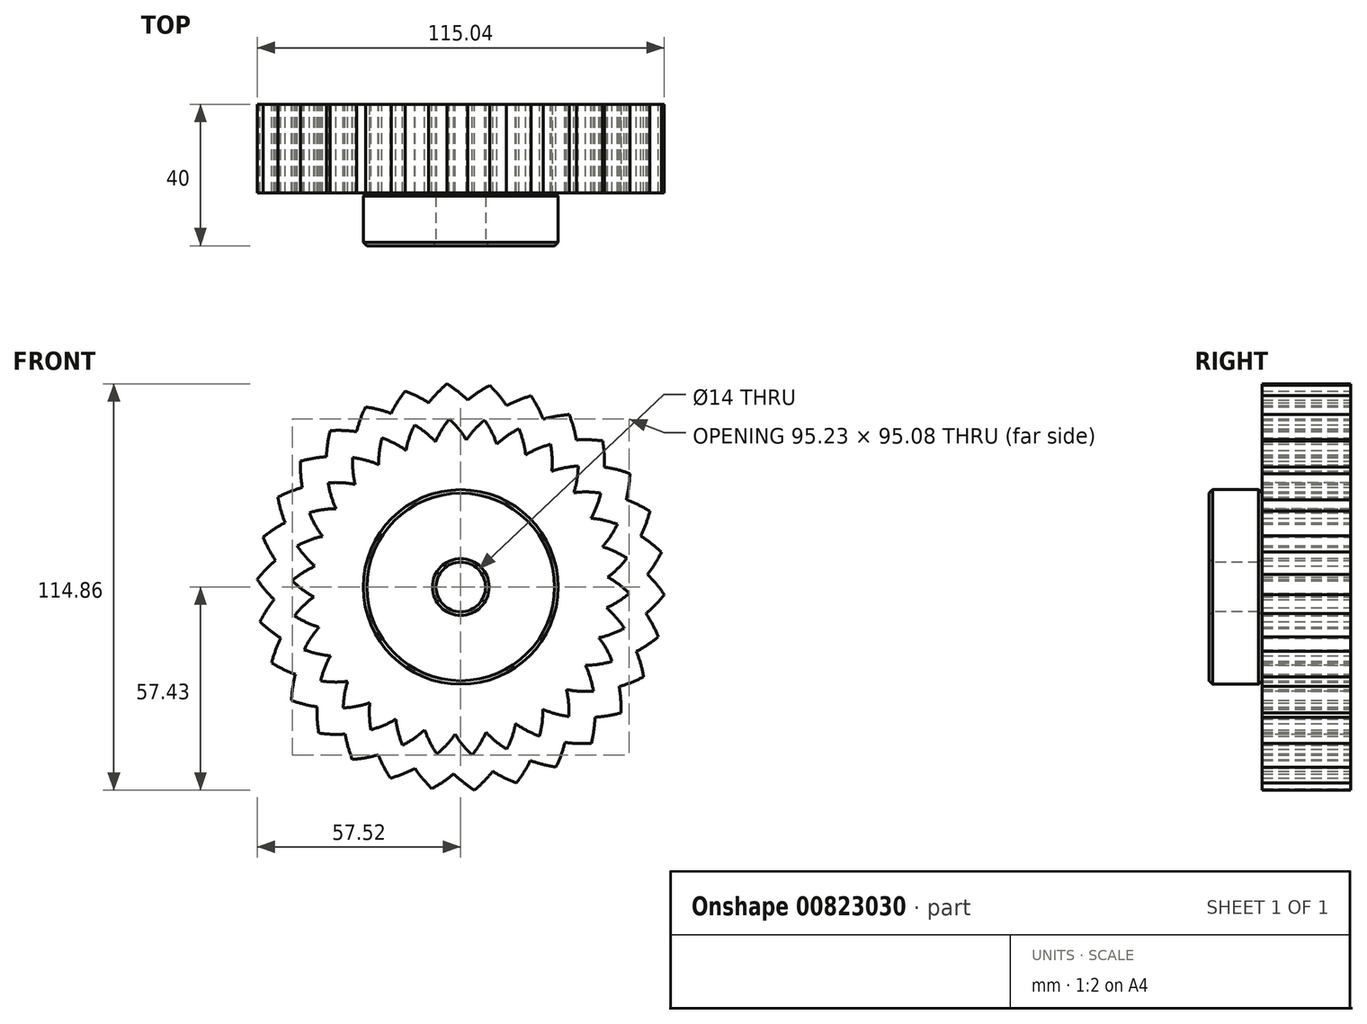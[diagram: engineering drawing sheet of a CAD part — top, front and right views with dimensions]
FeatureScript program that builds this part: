
annotation { "Feature Type Name" : "Feature", "Feature Type Description" : "" }
export const myFeature = defineFeature(function(context is Context, id is Id, definition is map)
    precondition{}
    {
        {
            var Q0;
            Q0=qCreatedBy(makeId("Front.planeOp"),FACE);
            var sketch = newSketch(context, id + "F0", { "sketchPlane" : qUnion([Q0])});
            skArc(sketch, "E0", {"start": v(-34.7, 6.12) * mm, "mid": v(-35.1, 3.07) * mm, "end": v(-35.24, 0) * mm, "construction": true});
            skLineSegment(sketch, "E1", {"start": v(0, 0) * mm, "end": v(309.01, 0) * mm, "construction": true});
            skPoint(sketch, "E2", {"position": v(35.24, 0) * mm});
            skLineSegment(sketch, "E3", {"start": v(0, 0) * mm, "end": v(-35.24, 0) * mm, "construction": true});
            skArc(sketch, "E4.trimOffspring", {"start": v(-30.6, -17.46) * mm, "mid": v(35.03, 3.83) * mm, "end": v(-33.66, 10.43) * mm, "construction": true});
            skFitSpline(sketch, "E5", {"points": [v(35.24, 0) * mm, v(35.77, 0.06) * mm, v(37.32, 0.5) * mm, v(39.74, 1.64) * mm, v(42.8, 3.8) * mm, v(46.2, 7.23) * mm, v(49.58, 12.07) * mm, v(52.5, 18.39) * mm, v(54.57, 26.16) * mm], "startDerivative": vector(10.04, 0.75) * mm, "endDerivative": vector(10.04, 44.08) * mm});
            skArc(sketch, "E6", {"start": v(34.12, 5.1) * mm, "mid": v(34, 5.9) * mm, "end": v(33.85, 6.7) * mm});
            skArc(sketch, "E7", {"start": v(39.96, 1.77) * mm, "mid": v(39.9, 2.68) * mm, "end": v(39.84, 3.6) * mm});
            skCircle(sketch, "E8", {"center": v(0, 0) * mm, "radius": 37.5 * mm, "construction": true});
            skPoint(sketch, "E9", {"position": v(37.5, 0.56) * mm});
            skPoint(sketch, "E10", {"position": v(36.56, 8.34) * mm});
            skPoint(sketch, "E11.orphan", {"position": v(37.03, 4.45) * mm});
            skLineSegment(sketch, "E12", {"start": v(37.5, 0.56) * mm, "end": v(37.03, 4.45) * mm, "construction": true});
            skLineSegment(sketch, "E13", {"start": v(37.26, 2.5) * mm, "end": v(0, 0) * mm, "construction": true});
            skFitSpline(sketch, "E14.MirrorCS", {"points": [v(34.92, 4.72) * mm, v(35.46, 4.73) * mm, v(37.05, 4.5) * mm, v(39.6, 3.7) * mm, v(42.93, 1.96) * mm, v(46.76, -0.98) * mm, v(50.74, -5.32) * mm, v(54.5, -11.2) * mm, v(57.58, -18.62) * mm], "startDerivative": vector(10.05, 0.6) * mm, "endDerivative": vector(15.85, -42.34) * mm});
            skLineSegment(sketch, "E15", {"start": v(35.24, 0) * mm, "end": v(35, 0) * mm});
            skLineSegment(sketch, "E16.MirrorCS", {"start": v(34.92, 4.72) * mm, "end": v(34.68, 4.68) * mm});
            skPoint(sketch, "E17.visualSharp", {"position": v(34.19, 4.62) * mm});
            skArc(sketch, "E17.filletArc", {"start": v(34.12, 5.1) * mm, "mid": v(34.31, 4.78) * mm, "end": v(34.68, 4.68) * mm});
            skPoint(sketch, "E18.visualSharp", {"position": v(34.5, 0) * mm});
            skArc(sketch, "E18.filletArc", {"start": v(35, 0) * mm, "mid": v(34.65, -0.14) * mm, "end": v(34.5, -0.5) * mm});
            skPoint(sketch, "E19.1.1", {"position": v(34.47, 7.33) * mm});
            skPoint(sketch, "E19.1.2", {"position": v(33.75, 7.17) * mm});
            skPoint(sketch, "E19.1.3", {"position": v(32.48, 11.62) * mm});
            skPoint(sketch, "E19.1.4", {"position": v(35.3, 12.05) * mm});
            skPoint(sketch, "E19.1.5", {"position": v(33.18, 11.87) * mm});
            skArc(sketch, "E19.1.6", {"start": v(38.72, 10.04) * mm, "mid": v(38.48, 10.92) * mm, "end": v(38.22, 11.8) * mm});
            skArc(sketch, "E19.1.8", {"start": v(32.31, 12.09) * mm, "mid": v(32.57, 11.8) * mm, "end": v(32.95, 11.8) * mm});
            skPoint(sketch, "E19.1.9", {"position": v(34.47, 7.33) * mm});
            skPoint(sketch, "E19.1.10", {"position": v(33.18, 11.87) * mm});
            skArc(sketch, "E19.1.11", {"start": v(34.23, 7.28) * mm, "mid": v(33.92, 7.06) * mm, "end": v(33.85, 6.7) * mm});
            skPoint(sketch, "E19.1.12", {"position": v(33.18, 11.87) * mm});
            skPoint(sketch, "E19.1.13", {"position": v(34.47, 7.33) * mm});
            skPoint(sketch, "E19.1.14", {"position": v(33.18, 11.87) * mm});
            skPoint(sketch, "E19.1.15", {"position": v(34.47, 7.33) * mm});
            skPoint(sketch, "E19.1.16", {"position": v(34.47, 7.33) * mm});
            skPoint(sketch, "E19.1.17", {"position": v(33.18, 11.87) * mm});
            skPoint(sketch, "E19.1.18", {"position": v(33.18, 11.87) * mm});
            skPoint(sketch, "E19.1.19", {"position": v(34.47, 7.33) * mm});
            skPoint(sketch, "E19.1.20", {"position": v(33.18, 11.87) * mm});
            skPoint(sketch, "E19.1.21", {"position": v(34.47, 7.33) * mm});
            skPoint(sketch, "E19.1.22", {"position": v(33.18, 11.87) * mm});
            skPoint(sketch, "E19.1.23", {"position": v(34.47, 7.33) * mm});
            skLineSegment(sketch, "E19.1.24", {"start": v(33.18, 11.87) * mm, "end": v(32.95, 11.8) * mm});
            skLineSegment(sketch, "E19.1.25", {"start": v(34.47, 7.33) * mm, "end": v(34.23, 7.28) * mm});
            skPoint(sketch, "E19.2.1", {"position": v(32.2, 14.33) * mm});
            skPoint(sketch, "E19.2.2", {"position": v(31.52, 14.03) * mm});
            skPoint(sketch, "E19.2.3", {"position": v(29.36, 18.12) * mm});
            skPoint(sketch, "E19.2.4", {"position": v(32.02, 19.13) * mm});
            skPoint(sketch, "E19.2.5", {"position": v(29.98, 18.51) * mm});
            skArc(sketch, "E19.2.6", {"start": v(35.79, 17.87) * mm, "mid": v(35.37, 18.68) * mm, "end": v(34.93, 19.49) * mm});
            skPoint(sketch, "E19.2.7", {"position": v(34.03, 15.76) * mm});
            skArc(sketch, "E19.2.8", {"start": v(29.1, 18.54) * mm, "mid": v(29.4, 18.32) * mm, "end": v(29.78, 18.38) * mm});
            skPoint(sketch, "E19.2.9", {"position": v(32.2, 14.33) * mm});
            skPoint(sketch, "E19.2.10", {"position": v(29.98, 18.51) * mm});
            skArc(sketch, "E19.2.11", {"start": v(31.97, 14.23) * mm, "mid": v(31.7, 13.96) * mm, "end": v(31.71, 13.58) * mm});
            skPoint(sketch, "E19.2.12", {"position": v(29.98, 18.51) * mm});
            skPoint(sketch, "E19.2.13", {"position": v(32.2, 14.33) * mm});
            skPoint(sketch, "E19.2.14", {"position": v(29.98, 18.51) * mm});
            skPoint(sketch, "E19.2.15", {"position": v(32.2, 14.33) * mm});
            skPoint(sketch, "E19.2.16", {"position": v(32.2, 14.33) * mm});
            skPoint(sketch, "E19.2.17", {"position": v(29.98, 18.51) * mm});
            skPoint(sketch, "E19.2.18", {"position": v(29.98, 18.51) * mm});
            skPoint(sketch, "E19.2.19", {"position": v(32.2, 14.33) * mm});
            skPoint(sketch, "E19.2.20", {"position": v(29.98, 18.51) * mm});
            skPoint(sketch, "E19.2.21", {"position": v(32.2, 14.33) * mm});
            skPoint(sketch, "E19.2.22", {"position": v(29.98, 18.51) * mm});
            skPoint(sketch, "E19.2.23", {"position": v(32.2, 14.33) * mm});
            skLineSegment(sketch, "E19.2.24", {"start": v(29.98, 18.51) * mm, "end": v(29.78, 18.38) * mm});
            skLineSegment(sketch, "E19.2.25", {"start": v(32.2, 14.33) * mm, "end": v(31.97, 14.23) * mm});
            skLineSegment(sketch, "E19.3.0", {"start": v(30, 22.5) * mm, "end": v(27.34, 25.37) * mm, "construction": true});
            skPoint(sketch, "E19.3.1", {"position": v(28.5, 20.71) * mm});
            skPoint(sketch, "E19.3.2", {"position": v(27.91, 20.28) * mm});
            skPoint(sketch, "E19.3.3", {"position": v(24.95, 23.83) * mm});
            skPoint(sketch, "E19.3.4", {"position": v(27.34, 25.37) * mm});
            skPoint(sketch, "E19.3.5", {"position": v(25.48, 24.34) * mm});
            skArc(sketch, "E19.3.6", {"start": v(31.29, 24.92) * mm, "mid": v(30.71, 25.63) * mm, "end": v(30.12, 26.32) * mm});
            skPoint(sketch, "E19.3.7", {"position": v(30, 22.5) * mm});
            skArc(sketch, "E19.3.8", {"start": v(24.6, 24.19) * mm, "mid": v(24.95, 24.04) * mm, "end": v(25.3, 24.17) * mm});
            skPoint(sketch, "E19.3.9", {"position": v(28.5, 20.71) * mm});
            skPoint(sketch, "E19.3.10", {"position": v(25.48, 24.34) * mm});
            skArc(sketch, "E19.3.11", {"start": v(28.31, 20.57) * mm, "mid": v(28.11, 20.25) * mm, "end": v(28.2, 19.88) * mm});
            skPoint(sketch, "E19.3.12", {"position": v(25.48, 24.34) * mm});
            skPoint(sketch, "E19.3.13", {"position": v(28.5, 20.71) * mm});
            skPoint(sketch, "E19.3.14", {"position": v(25.48, 24.34) * mm});
            skPoint(sketch, "E19.3.15", {"position": v(28.5, 20.71) * mm});
            skPoint(sketch, "E19.3.16", {"position": v(28.5, 20.71) * mm});
            skPoint(sketch, "E19.3.17", {"position": v(25.48, 24.34) * mm});
            skPoint(sketch, "E19.3.18", {"position": v(25.48, 24.34) * mm});
            skPoint(sketch, "E19.3.19", {"position": v(28.5, 20.71) * mm});
            skPoint(sketch, "E19.3.20", {"position": v(25.48, 24.34) * mm});
            skPoint(sketch, "E19.3.21", {"position": v(28.5, 20.71) * mm});
            skPoint(sketch, "E19.3.22", {"position": v(25.48, 24.34) * mm});
            skPoint(sketch, "E19.3.23", {"position": v(28.5, 20.71) * mm});
            skLineSegment(sketch, "E19.3.24", {"start": v(25.48, 24.34) * mm, "end": v(25.3, 24.17) * mm});
            skLineSegment(sketch, "E19.3.25", {"start": v(28.5, 20.71) * mm, "end": v(28.31, 20.57) * mm});
            skLineSegment(sketch, "E19.4.0", {"start": v(24.67, 28.24) * mm, "end": v(21.47, 30.5) * mm, "construction": true});
            skPoint(sketch, "E19.4.1", {"position": v(23.58, 26.19) * mm});
            skPoint(sketch, "E19.4.2", {"position": v(23.09, 25.64) * mm});
            skPoint(sketch, "E19.4.3", {"position": v(19.45, 28.5) * mm});
            skPoint(sketch, "E19.4.4", {"position": v(21.47, 30.5) * mm});
            skPoint(sketch, "E19.4.5", {"position": v(19.86, 29.1) * mm});
            skArc(sketch, "E19.4.6", {"start": v(25.42, 30.88) * mm, "mid": v(24.71, 31.45) * mm, "end": v(23.99, 32.01) * mm});
            skPoint(sketch, "E19.4.7", {"position": v(24.67, 28.24) * mm});
            skArc(sketch, "E19.4.8", {"start": v(19.04, 28.77) * mm, "mid": v(19.4, 28.7) * mm, "end": v(19.73, 28.9) * mm});
            skPoint(sketch, "E19.4.9", {"position": v(23.58, 26.19) * mm});
            skPoint(sketch, "E19.4.10", {"position": v(19.86, 29.1) * mm});
            skArc(sketch, "E19.4.11", {"start": v(23.42, 26) * mm, "mid": v(23.29, 25.65) * mm, "end": v(23.45, 25.3) * mm});
            skPoint(sketch, "E19.4.12", {"position": v(19.86, 29.1) * mm});
            skPoint(sketch, "E19.4.13", {"position": v(23.58, 26.19) * mm});
            skPoint(sketch, "E19.4.14", {"position": v(19.86, 29.1) * mm});
            skPoint(sketch, "E19.4.15", {"position": v(23.58, 26.19) * mm});
            skPoint(sketch, "E19.4.16", {"position": v(23.58, 26.19) * mm});
            skPoint(sketch, "E19.4.17", {"position": v(19.86, 29.1) * mm});
            skPoint(sketch, "E19.4.18", {"position": v(19.86, 29.1) * mm});
            skPoint(sketch, "E19.4.19", {"position": v(23.58, 26.19) * mm});
            skPoint(sketch, "E19.4.20", {"position": v(19.86, 29.1) * mm});
            skPoint(sketch, "E19.4.21", {"position": v(23.58, 26.19) * mm});
            skPoint(sketch, "E19.4.22", {"position": v(19.86, 29.1) * mm});
            skPoint(sketch, "E19.4.23", {"position": v(23.58, 26.19) * mm});
            skLineSegment(sketch, "E19.4.24", {"start": v(19.86, 29.1) * mm, "end": v(19.73, 28.9) * mm});
            skLineSegment(sketch, "E19.4.25", {"start": v(23.58, 26.19) * mm, "end": v(23.42, 26) * mm});
            skLineSegment(sketch, "E19.5.0", {"start": v(18.26, 32.75) * mm, "end": v(14.66, 34.3) * mm, "construction": true});
            skPoint(sketch, "E19.5.1", {"position": v(17.62, 30.52) * mm});
            skPoint(sketch, "E19.5.2", {"position": v(17.25, 29.88) * mm});
            skPoint(sketch, "E19.5.3", {"position": v(13.1, 31.92) * mm});
            skPoint(sketch, "E19.5.4", {"position": v(14.66, 34.3) * mm});
            skPoint(sketch, "E19.5.5", {"position": v(13.38, 32.6) * mm});
            skArc(sketch, "E19.5.6", {"start": v(18.45, 35.5) * mm, "mid": v(17.63, 35.9) * mm, "end": v(16.8, 36.3) * mm});
            skPoint(sketch, "E19.5.7", {"position": v(18.26, 32.75) * mm});
            skArc(sketch, "E19.5.8", {"start": v(12.64, 32.1) * mm, "mid": v(13.02, 32.1) * mm, "end": v(13.28, 32.38) * mm});
            skPoint(sketch, "E19.5.9", {"position": v(17.62, 30.52) * mm});
            skPoint(sketch, "E19.5.10", {"position": v(13.38, 32.6) * mm});
            skArc(sketch, "E19.5.11", {"start": v(17.5, 30.3) * mm, "mid": v(17.45, 29.93) * mm, "end": v(17.68, 29.63) * mm});
            skPoint(sketch, "E19.5.12", {"position": v(13.38, 32.6) * mm});
            skPoint(sketch, "E19.5.13", {"position": v(17.62, 30.52) * mm});
            skPoint(sketch, "E19.5.14", {"position": v(13.38, 32.6) * mm});
            skPoint(sketch, "E19.5.15", {"position": v(17.62, 30.52) * mm});
            skPoint(sketch, "E19.5.16", {"position": v(17.62, 30.52) * mm});
            skPoint(sketch, "E19.5.17", {"position": v(13.38, 32.6) * mm});
            skPoint(sketch, "E19.5.18", {"position": v(13.38, 32.6) * mm});
            skPoint(sketch, "E19.5.19", {"position": v(17.62, 30.52) * mm});
            skPoint(sketch, "E19.5.20", {"position": v(13.38, 32.6) * mm});
            skPoint(sketch, "E19.5.21", {"position": v(17.62, 30.52) * mm});
            skPoint(sketch, "E19.5.22", {"position": v(13.38, 32.6) * mm});
            skPoint(sketch, "E19.5.23", {"position": v(17.62, 30.52) * mm});
            skLineSegment(sketch, "E19.5.24", {"start": v(13.38, 32.6) * mm, "end": v(13.28, 32.38) * mm});
            skLineSegment(sketch, "E19.5.25", {"start": v(17.62, 30.52) * mm, "end": v(17.5, 30.3) * mm});
            skLineSegment(sketch, "E19.6.0", {"start": v(11.06, 35.83) * mm, "end": v(7.2, 36.6) * mm, "construction": true});
            skPoint(sketch, "E19.6.1", {"position": v(10.89, 33.51) * mm});
            skPoint(sketch, "E19.6.2", {"position": v(10.66, 32.81) * mm});
            skPoint(sketch, "E19.6.3", {"position": v(6.17, 33.94) * mm});
            skPoint(sketch, "E19.6.4", {"position": v(7.2, 36.6) * mm});
            skPoint(sketch, "E19.6.5", {"position": v(6.3, 34.67) * mm});
            skArc(sketch, "E19.6.6", {"start": v(10.67, 38.55) * mm, "mid": v(9.78, 38.79) * mm, "end": v(8.9, 39) * mm});
            skPoint(sketch, "E19.6.7", {"position": v(11.06, 35.83) * mm});
            skArc(sketch, "E19.6.8", {"start": v(5.69, 34.03) * mm, "mid": v(6.06, 34.11) * mm, "end": v(6.26, 34.43) * mm});
            skPoint(sketch, "E19.6.9", {"position": v(10.89, 33.51) * mm});
            skPoint(sketch, "E19.6.10", {"position": v(6.3, 34.67) * mm});
            skArc(sketch, "E19.6.11", {"start": v(10.81, 33.28) * mm, "mid": v(10.84, 32.9) * mm, "end": v(11.13, 32.66) * mm});
            skPoint(sketch, "E19.6.12", {"position": v(6.3, 34.67) * mm});
            skPoint(sketch, "E19.6.13", {"position": v(10.89, 33.51) * mm});
            skPoint(sketch, "E19.6.14", {"position": v(6.3, 34.67) * mm});
            skPoint(sketch, "E19.6.15", {"position": v(10.89, 33.51) * mm});
            skPoint(sketch, "E19.6.16", {"position": v(10.89, 33.51) * mm});
            skPoint(sketch, "E19.6.17", {"position": v(6.3, 34.67) * mm});
            skPoint(sketch, "E19.6.18", {"position": v(6.3, 34.67) * mm});
            skPoint(sketch, "E19.6.19", {"position": v(10.89, 33.51) * mm});
            skPoint(sketch, "E19.6.20", {"position": v(6.3, 34.67) * mm});
            skPoint(sketch, "E19.6.21", {"position": v(10.89, 33.51) * mm});
            skPoint(sketch, "E19.6.22", {"position": v(6.3, 34.67) * mm});
            skPoint(sketch, "E19.6.23", {"position": v(10.89, 33.51) * mm});
            skLineSegment(sketch, "E19.6.24", {"start": v(6.3, 34.67) * mm, "end": v(6.26, 34.43) * mm});
            skLineSegment(sketch, "E19.6.25", {"start": v(10.89, 33.51) * mm, "end": v(10.81, 33.28) * mm});
            skLineSegment(sketch, "E19.7.0", {"start": v(3.36, 37.35) * mm, "end": v(-0.56, 37.3) * mm, "construction": true});
            skPoint(sketch, "E19.7.1", {"position": v(3.68, 35.05) * mm});
            skPoint(sketch, "E19.7.2", {"position": v(3.6, 34.31) * mm});
            skPoint(sketch, "E19.7.3", {"position": v(-1.02, 34.48) * mm});
            skPoint(sketch, "E19.7.4", {"position": v(-0.56, 37.3) * mm});
            skPoint(sketch, "E19.7.5", {"position": v(-1.04, 35.22) * mm});
            skArc(sketch, "E19.7.6", {"start": v(2.42, 39.93) * mm, "mid": v(1.5, 39.97) * mm, "end": v(0.6, 40) * mm});
            skPoint(sketch, "E19.7.7", {"position": v(3.36, 37.35) * mm});
            skArc(sketch, "E19.7.8", {"start": v(-1.51, 34.47) * mm, "mid": v(-1.17, 34.63) * mm, "end": v(-1.03, 34.98) * mm});
            skPoint(sketch, "E19.7.9", {"position": v(3.68, 35.05) * mm});
            skPoint(sketch, "E19.7.10", {"position": v(-1.04, 35.22) * mm});
            skArc(sketch, "E19.7.11", {"start": v(3.66, 34.8) * mm, "mid": v(3.76, 34.44) * mm, "end": v(4.1, 34.26) * mm});
            skPoint(sketch, "E19.7.12", {"position": v(-1.04, 35.22) * mm});
            skPoint(sketch, "E19.7.13", {"position": v(3.68, 35.05) * mm});
            skPoint(sketch, "E19.7.14", {"position": v(-1.04, 35.22) * mm});
            skPoint(sketch, "E19.7.15", {"position": v(3.68, 35.05) * mm});
            skPoint(sketch, "E19.7.16", {"position": v(3.68, 35.05) * mm});
            skPoint(sketch, "E19.7.17", {"position": v(-1.04, 35.22) * mm});
            skPoint(sketch, "E19.7.18", {"position": v(-1.04, 35.22) * mm});
            skPoint(sketch, "E19.7.19", {"position": v(3.68, 35.05) * mm});
            skPoint(sketch, "E19.7.20", {"position": v(-1.04, 35.22) * mm});
            skPoint(sketch, "E19.7.21", {"position": v(3.68, 35.05) * mm});
            skPoint(sketch, "E19.7.22", {"position": v(-1.04, 35.22) * mm});
            skPoint(sketch, "E19.7.23", {"position": v(3.68, 35.05) * mm});
            skLineSegment(sketch, "E19.7.24", {"start": v(-1.04, 35.22) * mm, "end": v(-1.03, 34.98) * mm});
            skLineSegment(sketch, "E19.7.25", {"start": v(3.68, 35.05) * mm, "end": v(3.66, 34.8) * mm});
            skLineSegment(sketch, "E19.8.0", {"start": v(-4.47, 37.23) * mm, "end": v(-8.3, 36.36) * mm, "construction": true});
            skPoint(sketch, "E19.8.1", {"position": v(-3.68, 35.05) * mm});
            skPoint(sketch, "E19.8.2", {"position": v(-3.6, 34.31) * mm});
            skPoint(sketch, "E19.8.3", {"position": v(-8.17, 33.52) * mm});
            skPoint(sketch, "E19.8.4", {"position": v(-8.3, 36.36) * mm});
            skPoint(sketch, "E19.8.5", {"position": v(-8.34, 34.24) * mm});
            skArc(sketch, "E19.8.6", {"start": v(-5.94, 39.56) * mm, "mid": v(-6.84, 39.41) * mm, "end": v(-7.74, 39.24) * mm});
            skPoint(sketch, "E19.8.7", {"position": v(-4.47, 37.23) * mm});
            skArc(sketch, "E19.8.8", {"start": v(-8.64, 33.4) * mm, "mid": v(-8.34, 33.63) * mm, "end": v(-8.28, 34) * mm});
            skPoint(sketch, "E19.8.9", {"position": v(-3.68, 35.05) * mm});
            skPoint(sketch, "E19.8.10", {"position": v(-8.34, 34.24) * mm});
            skArc(sketch, "E19.8.11", {"start": v(-3.66, 34.8) * mm, "mid": v(-3.48, 34.47) * mm, "end": v(-3.12, 34.36) * mm});
            skPoint(sketch, "E19.8.12", {"position": v(-8.34, 34.24) * mm});
            skPoint(sketch, "E19.8.13", {"position": v(-3.68, 35.05) * mm});
            skPoint(sketch, "E19.8.14", {"position": v(-8.34, 34.24) * mm});
            skPoint(sketch, "E19.8.15", {"position": v(-3.68, 35.05) * mm});
            skPoint(sketch, "E19.8.16", {"position": v(-3.68, 35.05) * mm});
            skPoint(sketch, "E19.8.17", {"position": v(-8.34, 34.24) * mm});
            skPoint(sketch, "E19.8.18", {"position": v(-8.34, 34.24) * mm});
            skPoint(sketch, "E19.8.19", {"position": v(-3.68, 35.05) * mm});
            skPoint(sketch, "E19.8.20", {"position": v(-8.34, 34.24) * mm});
            skPoint(sketch, "E19.8.21", {"position": v(-3.68, 35.05) * mm});
            skPoint(sketch, "E19.8.22", {"position": v(-8.34, 34.24) * mm});
            skPoint(sketch, "E19.8.23", {"position": v(-3.68, 35.05) * mm});
            skLineSegment(sketch, "E19.8.24", {"start": v(-8.34, 34.24) * mm, "end": v(-8.28, 34) * mm});
            skLineSegment(sketch, "E19.8.25", {"start": v(-3.68, 35.05) * mm, "end": v(-3.66, 34.8) * mm});
            skLineSegment(sketch, "E19.9.0", {"start": v(-12.12, 35.49) * mm, "end": v(-15.67, 33.84) * mm, "construction": true});
            skPoint(sketch, "E19.9.1", {"position": v(-10.89, 33.51) * mm});
            skPoint(sketch, "E19.9.2", {"position": v(-10.66, 32.81) * mm});
            skPoint(sketch, "E19.9.3", {"position": v(-14.96, 31.09) * mm});
            skPoint(sketch, "E19.9.4", {"position": v(-15.67, 33.84) * mm});
            skPoint(sketch, "E19.9.5", {"position": v(-15.28, 31.76) * mm});
            skArc(sketch, "E19.9.6", {"start": v(-14.03, 37.46) * mm, "mid": v(-14.88, 37.13) * mm, "end": v(-15.73, 36.78) * mm});
            skPoint(sketch, "E19.9.7", {"position": v(-12.12, 35.49) * mm});
            skArc(sketch, "E19.9.8", {"start": v(-15.4, 30.87) * mm, "mid": v(-15.15, 31.16) * mm, "end": v(-15.17, 31.54) * mm});
            skPoint(sketch, "E19.9.9", {"position": v(-10.89, 33.51) * mm});
            skPoint(sketch, "E19.9.10", {"position": v(-15.28, 31.76) * mm});
            skArc(sketch, "E19.9.11", {"start": v(-10.81, 33.28) * mm, "mid": v(-10.57, 33) * mm, "end": v(-10.2, 32.96) * mm});
            skPoint(sketch, "E19.9.12", {"position": v(-15.28, 31.76) * mm});
            skPoint(sketch, "E19.9.13", {"position": v(-10.89, 33.51) * mm});
            skPoint(sketch, "E19.9.14", {"position": v(-15.28, 31.76) * mm});
            skPoint(sketch, "E19.9.15", {"position": v(-10.89, 33.51) * mm});
            skPoint(sketch, "E19.9.16", {"position": v(-10.89, 33.51) * mm});
            skPoint(sketch, "E19.9.17", {"position": v(-15.28, 31.76) * mm});
            skPoint(sketch, "E19.9.18", {"position": v(-15.28, 31.76) * mm});
            skPoint(sketch, "E19.9.19", {"position": v(-10.89, 33.51) * mm});
            skPoint(sketch, "E19.9.20", {"position": v(-15.28, 31.76) * mm});
            skPoint(sketch, "E19.9.21", {"position": v(-10.89, 33.51) * mm});
            skPoint(sketch, "E19.9.22", {"position": v(-15.28, 31.76) * mm});
            skPoint(sketch, "E19.9.23", {"position": v(-10.89, 33.51) * mm});
            skLineSegment(sketch, "E19.9.24", {"start": v(-15.28, 31.76) * mm, "end": v(-15.17, 31.54) * mm});
            skLineSegment(sketch, "E19.9.25", {"start": v(-10.89, 33.51) * mm, "end": v(-10.81, 33.28) * mm});
            skLineSegment(sketch, "E19.10.0", {"start": v(-19.23, 32.2) * mm, "end": v(-22.37, 29.84) * mm, "construction": true});
            skPoint(sketch, "E19.10.1", {"position": v(-17.62, 30.52) * mm});
            skPoint(sketch, "E19.10.2", {"position": v(-17.25, 29.88) * mm});
            skPoint(sketch, "E19.10.3", {"position": v(-21.1, 27.3) * mm});
            skPoint(sketch, "E19.10.4", {"position": v(-22.37, 29.84) * mm});
            skPoint(sketch, "E19.10.5", {"position": v(-21.54, 27.89) * mm});
            skArc(sketch, "E19.10.6", {"start": v(-21.51, 33.72) * mm, "mid": v(-22.28, 33.22) * mm, "end": v(-23.03, 32.7) * mm});
            skPoint(sketch, "E19.10.7", {"position": v(-19.23, 32.2) * mm});
            skArc(sketch, "E19.10.8", {"start": v(-21.48, 27) * mm, "mid": v(-21.3, 27.33) * mm, "end": v(-21.4, 27.7) * mm});
            skPoint(sketch, "E19.10.9", {"position": v(-17.62, 30.52) * mm});
            skPoint(sketch, "E19.10.10", {"position": v(-21.54, 27.89) * mm});
            skArc(sketch, "E19.10.11", {"start": v(-17.5, 30.3) * mm, "mid": v(-17.2, 30.08) * mm, "end": v(-16.82, 30.12) * mm});
            skPoint(sketch, "E19.10.12", {"position": v(-21.54, 27.89) * mm});
            skPoint(sketch, "E19.10.13", {"position": v(-17.62, 30.52) * mm});
            skPoint(sketch, "E19.10.14", {"position": v(-21.54, 27.89) * mm});
            skPoint(sketch, "E19.10.15", {"position": v(-17.62, 30.52) * mm});
            skPoint(sketch, "E19.10.16", {"position": v(-17.62, 30.52) * mm});
            skPoint(sketch, "E19.10.17", {"position": v(-21.54, 27.89) * mm});
            skPoint(sketch, "E19.10.18", {"position": v(-21.54, 27.89) * mm});
            skPoint(sketch, "E19.10.19", {"position": v(-17.62, 30.52) * mm});
            skPoint(sketch, "E19.10.20", {"position": v(-21.54, 27.89) * mm});
            skPoint(sketch, "E19.10.21", {"position": v(-17.62, 30.52) * mm});
            skPoint(sketch, "E19.10.22", {"position": v(-21.54, 27.89) * mm});
            skPoint(sketch, "E19.10.23", {"position": v(-17.62, 30.52) * mm});
            skLineSegment(sketch, "E19.10.24", {"start": v(-21.54, 27.89) * mm, "end": v(-21.4, 27.7) * mm});
            skLineSegment(sketch, "E19.10.25", {"start": v(-17.62, 30.52) * mm, "end": v(-17.5, 30.3) * mm});
            skLineSegment(sketch, "E19.11.0", {"start": v(-25.5, 27.5) * mm, "end": v(-28.08, 24.54) * mm, "construction": true});
            skPoint(sketch, "E19.11.1", {"position": v(-23.58, 26.19) * mm});
            skPoint(sketch, "E19.11.2", {"position": v(-23.09, 25.64) * mm});
            skPoint(sketch, "E19.11.3", {"position": v(-26.3, 22.32) * mm});
            skPoint(sketch, "E19.11.4", {"position": v(-28.08, 24.54) * mm});
            skPoint(sketch, "E19.11.5", {"position": v(-26.87, 22.8) * mm});
            skArc(sketch, "E19.11.6", {"start": v(-28.05, 28.51) * mm, "mid": v(-28.7, 27.86) * mm, "end": v(-29.33, 27.2) * mm});
            skPoint(sketch, "E19.11.7", {"position": v(-25.5, 27.5) * mm});
            skArc(sketch, "E19.11.8", {"start": v(-26.62, 21.94) * mm, "mid": v(-26.51, 22.3) * mm, "end": v(-26.69, 22.64) * mm});
            skPoint(sketch, "E19.11.9", {"position": v(-23.58, 26.19) * mm});
            skPoint(sketch, "E19.11.10", {"position": v(-26.87, 22.8) * mm});
            skArc(sketch, "E19.11.11", {"start": v(-23.42, 26) * mm, "mid": v(-23.08, 25.84) * mm, "end": v(-22.72, 25.97) * mm});
            skPoint(sketch, "E19.11.12", {"position": v(-26.87, 22.8) * mm});
            skPoint(sketch, "E19.11.13", {"position": v(-23.58, 26.19) * mm});
            skPoint(sketch, "E19.11.14", {"position": v(-26.87, 22.8) * mm});
            skPoint(sketch, "E19.11.15", {"position": v(-23.58, 26.19) * mm});
            skPoint(sketch, "E19.11.16", {"position": v(-23.58, 26.19) * mm});
            skPoint(sketch, "E19.11.17", {"position": v(-26.87, 22.8) * mm});
            skPoint(sketch, "E19.11.18", {"position": v(-26.87, 22.8) * mm});
            skPoint(sketch, "E19.11.19", {"position": v(-23.58, 26.19) * mm});
            skPoint(sketch, "E19.11.20", {"position": v(-26.87, 22.8) * mm});
            skPoint(sketch, "E19.11.21", {"position": v(-23.58, 26.19) * mm});
            skPoint(sketch, "E19.11.22", {"position": v(-26.87, 22.8) * mm});
            skPoint(sketch, "E19.11.23", {"position": v(-23.58, 26.19) * mm});
            skLineSegment(sketch, "E19.11.24", {"start": v(-26.87, 22.8) * mm, "end": v(-26.69, 22.64) * mm});
            skLineSegment(sketch, "E19.11.25", {"start": v(-23.58, 26.19) * mm, "end": v(-23.42, 26) * mm});
            skLineSegment(sketch, "E19.12.0", {"start": v(-30.66, 21.59) * mm, "end": v(-32.57, 18.16) * mm, "construction": true});
            skPoint(sketch, "E19.12.1", {"position": v(-28.5, 20.71) * mm});
            skPoint(sketch, "E19.12.2", {"position": v(-27.91, 20.28) * mm});
            skPoint(sketch, "E19.12.3", {"position": v(-30.37, 16.36) * mm});
            skPoint(sketch, "E19.12.4", {"position": v(-32.57, 18.16) * mm});
            skPoint(sketch, "E19.12.5", {"position": v(-31.02, 16.71) * mm});
            skArc(sketch, "E19.12.6", {"start": v(-33.37, 22.06) * mm, "mid": v(-33.86, 21.29) * mm, "end": v(-34.34, 20.5) * mm});
            skPoint(sketch, "E19.12.7", {"position": v(-30.66, 21.59) * mm});
            skArc(sketch, "E19.12.8", {"start": v(-30.6, 15.93) * mm, "mid": v(-30.57, 16.3) * mm, "end": v(-30.81, 16.6) * mm});
            skPoint(sketch, "E19.12.9", {"position": v(-28.5, 20.71) * mm});
            skPoint(sketch, "E19.12.10", {"position": v(-31.02, 16.71) * mm});
            skArc(sketch, "E19.12.11", {"start": v(-28.31, 20.57) * mm, "mid": v(-27.94, 20.48) * mm, "end": v(-27.62, 20.68) * mm});
            skPoint(sketch, "E19.12.12", {"position": v(-31.02, 16.71) * mm});
            skPoint(sketch, "E19.12.13", {"position": v(-28.5, 20.71) * mm});
            skPoint(sketch, "E19.12.14", {"position": v(-31.02, 16.71) * mm});
            skPoint(sketch, "E19.12.15", {"position": v(-28.5, 20.71) * mm});
            skPoint(sketch, "E19.12.16", {"position": v(-28.5, 20.71) * mm});
            skPoint(sketch, "E19.12.17", {"position": v(-31.02, 16.71) * mm});
            skPoint(sketch, "E19.12.18", {"position": v(-31.02, 16.71) * mm});
            skPoint(sketch, "E19.12.19", {"position": v(-28.5, 20.71) * mm});
            skPoint(sketch, "E19.12.20", {"position": v(-31.02, 16.71) * mm});
            skPoint(sketch, "E19.12.21", {"position": v(-28.5, 20.71) * mm});
            skPoint(sketch, "E19.12.22", {"position": v(-31.02, 16.71) * mm});
            skPoint(sketch, "E19.12.23", {"position": v(-28.5, 20.71) * mm});
            skLineSegment(sketch, "E19.12.24", {"start": v(-31.02, 16.71) * mm, "end": v(-30.81, 16.6) * mm});
            skLineSegment(sketch, "E19.12.25", {"start": v(-28.5, 20.71) * mm, "end": v(-28.31, 20.57) * mm});
            skLineSegment(sketch, "E19.13.0", {"start": v(-34.48, 14.74) * mm, "end": v(-35.64, 11) * mm, "construction": true});
            skPoint(sketch, "E19.13.1", {"position": v(-32.2, 14.33) * mm});
            skPoint(sketch, "E19.13.2", {"position": v(-31.52, 14.03) * mm});
            skPoint(sketch, "E19.13.3", {"position": v(-33.11, 9.69) * mm});
            skPoint(sketch, "E19.13.4", {"position": v(-35.64, 11) * mm});
            skPoint(sketch, "E19.13.5", {"position": v(-33.82, 9.9) * mm});
            skArc(sketch, "E19.13.6", {"start": v(-37.23, 14.64) * mm, "mid": v(-37.55, 13.78) * mm, "end": v(-37.86, 12.92) * mm});
            skPoint(sketch, "E19.13.7", {"position": v(-34.48, 14.74) * mm});
            skArc(sketch, "E19.13.8", {"start": v(-33.25, 9.21) * mm, "mid": v(-33.3, 9.6) * mm, "end": v(-33.59, 9.83) * mm});
            skPoint(sketch, "E19.13.9", {"position": v(-32.2, 14.33) * mm});
            skPoint(sketch, "E19.13.10", {"position": v(-33.82, 9.9) * mm});
            skArc(sketch, "E19.13.11", {"start": v(-31.97, 14.23) * mm, "mid": v(-31.6, 14.22) * mm, "end": v(-31.31, 14.48) * mm});
            skPoint(sketch, "E19.13.12", {"position": v(-33.82, 9.9) * mm});
            skPoint(sketch, "E19.13.13", {"position": v(-32.2, 14.33) * mm});
            skPoint(sketch, "E19.13.14", {"position": v(-33.82, 9.9) * mm});
            skPoint(sketch, "E19.13.15", {"position": v(-32.2, 14.33) * mm});
            skPoint(sketch, "E19.13.16", {"position": v(-32.2, 14.33) * mm});
            skPoint(sketch, "E19.13.17", {"position": v(-33.82, 9.9) * mm});
            skPoint(sketch, "E19.13.18", {"position": v(-33.82, 9.9) * mm});
            skPoint(sketch, "E19.13.19", {"position": v(-32.2, 14.33) * mm});
            skPoint(sketch, "E19.13.20", {"position": v(-33.82, 9.9) * mm});
            skPoint(sketch, "E19.13.21", {"position": v(-32.2, 14.33) * mm});
            skPoint(sketch, "E19.13.22", {"position": v(-33.82, 9.9) * mm});
            skPoint(sketch, "E19.13.23", {"position": v(-32.2, 14.33) * mm});
            skLineSegment(sketch, "E19.13.24", {"start": v(-33.82, 9.9) * mm, "end": v(-33.59, 9.83) * mm});
            skLineSegment(sketch, "E19.13.25", {"start": v(-32.2, 14.33) * mm, "end": v(-31.97, 14.23) * mm});
            skLineSegment(sketch, "E19.14.0", {"start": v(-36.8, 7.25) * mm, "end": v(-37.14, 3.35) * mm, "construction": true});
            skPoint(sketch, "E19.14.1", {"position": v(-34.47, 7.33) * mm});
            skPoint(sketch, "E19.14.2", {"position": v(-33.75, 7.17) * mm});
            skPoint(sketch, "E19.14.3", {"position": v(-34.4, 2.6) * mm});
            skPoint(sketch, "E19.14.4", {"position": v(-37.14, 3.35) * mm});
            skPoint(sketch, "E19.14.5", {"position": v(-35.14, 2.65) * mm});
            skArc(sketch, "E19.14.6", {"start": v(-39.46, 6.58) * mm, "mid": v(-39.6, 5.67) * mm, "end": v(-39.71, 4.77) * mm});
            skPoint(sketch, "E19.14.7", {"position": v(-36.8, 7.25) * mm});
            skArc(sketch, "E19.14.8", {"start": v(-34.44, 2.1) * mm, "mid": v(-34.56, 2.46) * mm, "end": v(-34.9, 2.63) * mm});
            skPoint(sketch, "E19.14.9", {"position": v(-34.47, 7.33) * mm});
            skPoint(sketch, "E19.14.10", {"position": v(-35.14, 2.65) * mm});
            skArc(sketch, "E19.14.11", {"start": v(-34.23, 7.28) * mm, "mid": v(-33.86, 7.34) * mm, "end": v(-33.64, 7.65) * mm});
            skPoint(sketch, "E19.14.12", {"position": v(-35.14, 2.65) * mm});
            skPoint(sketch, "E19.14.13", {"position": v(-34.47, 7.33) * mm});
            skPoint(sketch, "E19.14.14", {"position": v(-35.14, 2.65) * mm});
            skPoint(sketch, "E19.14.15", {"position": v(-34.47, 7.33) * mm});
            skPoint(sketch, "E19.14.16", {"position": v(-34.47, 7.33) * mm});
            skPoint(sketch, "E19.14.17", {"position": v(-35.14, 2.65) * mm});
            skPoint(sketch, "E19.14.18", {"position": v(-35.14, 2.65) * mm});
            skPoint(sketch, "E19.14.19", {"position": v(-34.47, 7.33) * mm});
            skPoint(sketch, "E19.14.20", {"position": v(-35.14, 2.65) * mm});
            skPoint(sketch, "E19.14.21", {"position": v(-34.47, 7.33) * mm});
            skPoint(sketch, "E19.14.22", {"position": v(-35.14, 2.65) * mm});
            skPoint(sketch, "E19.14.23", {"position": v(-34.47, 7.33) * mm});
            skLineSegment(sketch, "E19.14.24", {"start": v(-35.14, 2.65) * mm, "end": v(-34.9, 2.63) * mm});
            skLineSegment(sketch, "E19.14.25", {"start": v(-34.47, 7.33) * mm, "end": v(-34.23, 7.28) * mm});
            skLineSegment(sketch, "E19.15.0", {"start": v(-37.5, -0.56) * mm, "end": v(-37.03, -4.45) * mm, "construction": true});
            skPoint(sketch, "E19.15.1", {"position": v(-35.24, 0) * mm});
            skPoint(sketch, "E19.15.2", {"position": v(-34.5, 0) * mm});
            skPoint(sketch, "E19.15.3", {"position": v(-34.19, -4.62) * mm});
            skPoint(sketch, "E19.15.4", {"position": v(-37.03, -4.45) * mm});
            skPoint(sketch, "E19.15.5", {"position": v(-34.92, -4.72) * mm});
            skArc(sketch, "E19.15.6", {"start": v(-39.96, -1.77) * mm, "mid": v(-39.9, -2.68) * mm, "end": v(-39.84, -3.6) * mm});
            skPoint(sketch, "E19.15.7", {"position": v(-37.5, -0.56) * mm});
            skArc(sketch, "E19.15.8", {"start": v(-34.12, -5.1) * mm, "mid": v(-34.31, -4.78) * mm, "end": v(-34.68, -4.68) * mm});
            skPoint(sketch, "E19.15.9", {"position": v(-35.24, 0) * mm});
            skPoint(sketch, "E19.15.10", {"position": v(-34.92, -4.72) * mm});
            skArc(sketch, "E19.15.11", {"start": v(-35, 0) * mm, "mid": v(-34.65, 0.14) * mm, "end": v(-34.5, 0.5) * mm});
            skPoint(sketch, "E19.15.12", {"position": v(-34.92, -4.72) * mm});
            skPoint(sketch, "E19.15.13", {"position": v(-35.24, 0) * mm});
            skPoint(sketch, "E19.15.14", {"position": v(-34.92, -4.72) * mm});
            skPoint(sketch, "E19.15.15", {"position": v(-35.24, 0) * mm});
            skPoint(sketch, "E19.15.16", {"position": v(-35.24, 0) * mm});
            skPoint(sketch, "E19.15.17", {"position": v(-34.92, -4.72) * mm});
            skPoint(sketch, "E19.15.18", {"position": v(-34.92, -4.72) * mm});
            skPoint(sketch, "E19.15.19", {"position": v(-35.24, 0) * mm});
            skPoint(sketch, "E19.15.20", {"position": v(-34.92, -4.72) * mm});
            skPoint(sketch, "E19.15.21", {"position": v(-35.24, 0) * mm});
            skPoint(sketch, "E19.15.22", {"position": v(-34.92, -4.72) * mm});
            skPoint(sketch, "E19.15.23", {"position": v(-35.24, 0) * mm});
            skLineSegment(sketch, "E19.15.24", {"start": v(-34.92, -4.72) * mm, "end": v(-34.68, -4.68) * mm});
            skLineSegment(sketch, "E19.15.25", {"start": v(-35.24, 0) * mm, "end": v(-35, 0) * mm});
            skLineSegment(sketch, "E19.16.0", {"start": v(-36.56, -8.34) * mm, "end": v(-35.3, -12.05) * mm, "construction": true});
            skPoint(sketch, "E19.16.1", {"position": v(-34.47, -7.33) * mm});
            skPoint(sketch, "E19.16.2", {"position": v(-33.75, -7.17) * mm});
            skPoint(sketch, "E19.16.3", {"position": v(-32.48, -11.62) * mm});
            skPoint(sketch, "E19.16.4", {"position": v(-35.3, -12.05) * mm});
            skPoint(sketch, "E19.16.5", {"position": v(-33.18, -11.87) * mm});
            skArc(sketch, "E19.16.6", {"start": v(-38.72, -10.04) * mm, "mid": v(-38.48, -10.92) * mm, "end": v(-38.22, -11.8) * mm});
            skPoint(sketch, "E19.16.7", {"position": v(-36.56, -8.34) * mm});
            skArc(sketch, "E19.16.8", {"start": v(-32.31, -12.09) * mm, "mid": v(-32.57, -11.8) * mm, "end": v(-32.95, -11.8) * mm});
            skPoint(sketch, "E19.16.9", {"position": v(-34.47, -7.33) * mm});
            skPoint(sketch, "E19.16.10", {"position": v(-33.18, -11.87) * mm});
            skArc(sketch, "E19.16.11", {"start": v(-34.23, -7.28) * mm, "mid": v(-33.92, -7.06) * mm, "end": v(-33.85, -6.7) * mm});
            skPoint(sketch, "E19.16.12", {"position": v(-33.18, -11.87) * mm});
            skPoint(sketch, "E19.16.13", {"position": v(-34.47, -7.33) * mm});
            skPoint(sketch, "E19.16.14", {"position": v(-33.18, -11.87) * mm});
            skPoint(sketch, "E19.16.15", {"position": v(-34.47, -7.33) * mm});
            skPoint(sketch, "E19.16.16", {"position": v(-34.47, -7.33) * mm});
            skPoint(sketch, "E19.16.17", {"position": v(-33.18, -11.87) * mm});
            skPoint(sketch, "E19.16.18", {"position": v(-33.18, -11.87) * mm});
            skPoint(sketch, "E19.16.19", {"position": v(-34.47, -7.33) * mm});
            skPoint(sketch, "E19.16.20", {"position": v(-33.18, -11.87) * mm});
            skPoint(sketch, "E19.16.21", {"position": v(-34.47, -7.33) * mm});
            skPoint(sketch, "E19.16.22", {"position": v(-33.18, -11.87) * mm});
            skPoint(sketch, "E19.16.23", {"position": v(-34.47, -7.33) * mm});
            skLineSegment(sketch, "E19.16.24", {"start": v(-33.18, -11.87) * mm, "end": v(-32.95, -11.8) * mm});
            skLineSegment(sketch, "E19.16.25", {"start": v(-34.47, -7.33) * mm, "end": v(-34.23, -7.28) * mm});
            skLineSegment(sketch, "E19.17.0", {"start": v(-34.03, -15.76) * mm, "end": v(-32.02, -19.13) * mm, "construction": true});
            skPoint(sketch, "E19.17.1", {"position": v(-32.2, -14.33) * mm});
            skPoint(sketch, "E19.17.2", {"position": v(-31.52, -14.03) * mm});
            skPoint(sketch, "E19.17.3", {"position": v(-29.36, -18.12) * mm});
            skPoint(sketch, "E19.17.4", {"position": v(-32.02, -19.13) * mm});
            skPoint(sketch, "E19.17.5", {"position": v(-29.98, -18.51) * mm});
            skArc(sketch, "E19.17.6", {"start": v(-35.79, -17.87) * mm, "mid": v(-35.37, -18.68) * mm, "end": v(-34.93, -19.49) * mm});
            skPoint(sketch, "E19.17.7", {"position": v(-34.03, -15.76) * mm});
            skArc(sketch, "E19.17.8", {"start": v(-29.1, -18.54) * mm, "mid": v(-29.4, -18.32) * mm, "end": v(-29.78, -18.38) * mm});
            skPoint(sketch, "E19.17.9", {"position": v(-32.2, -14.33) * mm});
            skPoint(sketch, "E19.17.10", {"position": v(-29.98, -18.51) * mm});
            skArc(sketch, "E19.17.11", {"start": v(-31.97, -14.23) * mm, "mid": v(-31.7, -13.96) * mm, "end": v(-31.71, -13.58) * mm});
            skPoint(sketch, "E19.17.12", {"position": v(-29.98, -18.51) * mm});
            skPoint(sketch, "E19.17.13", {"position": v(-32.2, -14.33) * mm});
            skPoint(sketch, "E19.17.14", {"position": v(-29.98, -18.51) * mm});
            skPoint(sketch, "E19.17.15", {"position": v(-32.2, -14.33) * mm});
            skPoint(sketch, "E19.17.16", {"position": v(-32.2, -14.33) * mm});
            skPoint(sketch, "E19.17.17", {"position": v(-29.98, -18.51) * mm});
            skPoint(sketch, "E19.17.18", {"position": v(-29.98, -18.51) * mm});
            skPoint(sketch, "E19.17.19", {"position": v(-32.2, -14.33) * mm});
            skPoint(sketch, "E19.17.20", {"position": v(-29.98, -18.51) * mm});
            skPoint(sketch, "E19.17.21", {"position": v(-32.2, -14.33) * mm});
            skPoint(sketch, "E19.17.22", {"position": v(-29.98, -18.51) * mm});
            skPoint(sketch, "E19.17.23", {"position": v(-32.2, -14.33) * mm});
            skLineSegment(sketch, "E19.17.24", {"start": v(-29.98, -18.51) * mm, "end": v(-29.78, -18.38) * mm});
            skLineSegment(sketch, "E19.17.25", {"start": v(-32.2, -14.33) * mm, "end": v(-31.97, -14.23) * mm});
            skLineSegment(sketch, "E19.18.0", {"start": v(-30, -22.5) * mm, "end": v(-27.34, -25.37) * mm, "construction": true});
            skPoint(sketch, "E19.18.1", {"position": v(-28.5, -20.71) * mm});
            skPoint(sketch, "E19.18.2", {"position": v(-27.91, -20.28) * mm});
            skPoint(sketch, "E19.18.3", {"position": v(-24.95, -23.83) * mm});
            skPoint(sketch, "E19.18.4", {"position": v(-27.34, -25.37) * mm});
            skPoint(sketch, "E19.18.5", {"position": v(-25.48, -24.34) * mm});
            skArc(sketch, "E19.18.6", {"start": v(-31.29, -24.92) * mm, "mid": v(-30.71, -25.63) * mm, "end": v(-30.12, -26.32) * mm});
            skPoint(sketch, "E19.18.7", {"position": v(-30, -22.5) * mm});
            skArc(sketch, "E19.18.8", {"start": v(-24.6, -24.19) * mm, "mid": v(-24.95, -24.04) * mm, "end": v(-25.3, -24.17) * mm});
            skPoint(sketch, "E19.18.9", {"position": v(-28.5, -20.71) * mm});
            skPoint(sketch, "E19.18.10", {"position": v(-25.48, -24.34) * mm});
            skArc(sketch, "E19.18.11", {"start": v(-28.31, -20.57) * mm, "mid": v(-28.11, -20.25) * mm, "end": v(-28.2, -19.88) * mm});
            skPoint(sketch, "E19.18.12", {"position": v(-25.48, -24.34) * mm});
            skPoint(sketch, "E19.18.13", {"position": v(-28.5, -20.71) * mm});
            skPoint(sketch, "E19.18.14", {"position": v(-25.48, -24.34) * mm});
            skPoint(sketch, "E19.18.15", {"position": v(-28.5, -20.71) * mm});
            skPoint(sketch, "E19.18.16", {"position": v(-28.5, -20.71) * mm});
            skPoint(sketch, "E19.18.17", {"position": v(-25.48, -24.34) * mm});
            skPoint(sketch, "E19.18.18", {"position": v(-25.48, -24.34) * mm});
            skPoint(sketch, "E19.18.19", {"position": v(-28.5, -20.71) * mm});
            skPoint(sketch, "E19.18.20", {"position": v(-25.48, -24.34) * mm});
            skPoint(sketch, "E19.18.21", {"position": v(-28.5, -20.71) * mm});
            skPoint(sketch, "E19.18.22", {"position": v(-25.48, -24.34) * mm});
            skPoint(sketch, "E19.18.23", {"position": v(-28.5, -20.71) * mm});
            skLineSegment(sketch, "E19.18.24", {"start": v(-25.48, -24.34) * mm, "end": v(-25.3, -24.17) * mm});
            skLineSegment(sketch, "E19.18.25", {"start": v(-28.5, -20.71) * mm, "end": v(-28.31, -20.57) * mm});
            skLineSegment(sketch, "E19.19.0", {"start": v(-24.67, -28.24) * mm, "end": v(-21.47, -30.5) * mm, "construction": true});
            skPoint(sketch, "E19.19.1", {"position": v(-23.58, -26.19) * mm});
            skPoint(sketch, "E19.19.2", {"position": v(-23.09, -25.64) * mm});
            skPoint(sketch, "E19.19.3", {"position": v(-19.45, -28.5) * mm});
            skPoint(sketch, "E19.19.4", {"position": v(-21.47, -30.5) * mm});
            skPoint(sketch, "E19.19.5", {"position": v(-19.86, -29.1) * mm});
            skArc(sketch, "E19.19.6", {"start": v(-25.42, -30.88) * mm, "mid": v(-24.71, -31.45) * mm, "end": v(-23.99, -32.01) * mm});
            skPoint(sketch, "E19.19.7", {"position": v(-24.67, -28.24) * mm});
            skArc(sketch, "E19.19.8", {"start": v(-19.04, -28.77) * mm, "mid": v(-19.4, -28.7) * mm, "end": v(-19.73, -28.9) * mm});
            skPoint(sketch, "E19.19.9", {"position": v(-23.58, -26.19) * mm});
            skPoint(sketch, "E19.19.10", {"position": v(-19.86, -29.1) * mm});
            skArc(sketch, "E19.19.11", {"start": v(-23.42, -26) * mm, "mid": v(-23.29, -25.65) * mm, "end": v(-23.45, -25.3) * mm});
            skPoint(sketch, "E19.19.12", {"position": v(-19.86, -29.1) * mm});
            skPoint(sketch, "E19.19.13", {"position": v(-23.58, -26.19) * mm});
            skPoint(sketch, "E19.19.14", {"position": v(-19.86, -29.1) * mm});
            skPoint(sketch, "E19.19.15", {"position": v(-23.58, -26.19) * mm});
            skPoint(sketch, "E19.19.16", {"position": v(-23.58, -26.19) * mm});
            skPoint(sketch, "E19.19.17", {"position": v(-19.86, -29.1) * mm});
            skPoint(sketch, "E19.19.18", {"position": v(-19.86, -29.1) * mm});
            skPoint(sketch, "E19.19.19", {"position": v(-23.58, -26.19) * mm});
            skPoint(sketch, "E19.19.20", {"position": v(-19.86, -29.1) * mm});
            skPoint(sketch, "E19.19.21", {"position": v(-23.58, -26.19) * mm});
            skPoint(sketch, "E19.19.22", {"position": v(-19.86, -29.1) * mm});
            skPoint(sketch, "E19.19.23", {"position": v(-23.58, -26.19) * mm});
            skLineSegment(sketch, "E19.19.24", {"start": v(-19.86, -29.1) * mm, "end": v(-19.73, -28.9) * mm});
            skLineSegment(sketch, "E19.19.25", {"start": v(-23.58, -26.19) * mm, "end": v(-23.42, -26) * mm});
            skLineSegment(sketch, "E19.20.0", {"start": v(-18.26, -32.75) * mm, "end": v(-14.66, -34.3) * mm, "construction": true});
            skPoint(sketch, "E19.20.1", {"position": v(-17.62, -30.52) * mm});
            skPoint(sketch, "E19.20.2", {"position": v(-17.25, -29.88) * mm});
            skPoint(sketch, "E19.20.3", {"position": v(-13.1, -31.92) * mm});
            skPoint(sketch, "E19.20.4", {"position": v(-14.66, -34.3) * mm});
            skPoint(sketch, "E19.20.5", {"position": v(-13.38, -32.6) * mm});
            skArc(sketch, "E19.20.6", {"start": v(-18.45, -35.5) * mm, "mid": v(-17.63, -35.9) * mm, "end": v(-16.8, -36.3) * mm});
            skPoint(sketch, "E19.20.7", {"position": v(-18.26, -32.75) * mm});
            skArc(sketch, "E19.20.8", {"start": v(-12.64, -32.1) * mm, "mid": v(-13.02, -32.1) * mm, "end": v(-13.28, -32.38) * mm});
            skPoint(sketch, "E19.20.9", {"position": v(-17.62, -30.52) * mm});
            skPoint(sketch, "E19.20.10", {"position": v(-13.38, -32.6) * mm});
            skArc(sketch, "E19.20.11", {"start": v(-17.5, -30.3) * mm, "mid": v(-17.45, -29.93) * mm, "end": v(-17.68, -29.63) * mm});
            skPoint(sketch, "E19.20.12", {"position": v(-13.38, -32.6) * mm});
            skPoint(sketch, "E19.20.13", {"position": v(-17.62, -30.52) * mm});
            skPoint(sketch, "E19.20.14", {"position": v(-13.38, -32.6) * mm});
            skPoint(sketch, "E19.20.15", {"position": v(-17.62, -30.52) * mm});
            skPoint(sketch, "E19.20.16", {"position": v(-17.62, -30.52) * mm});
            skPoint(sketch, "E19.20.17", {"position": v(-13.38, -32.6) * mm});
            skPoint(sketch, "E19.20.18", {"position": v(-13.38, -32.6) * mm});
            skPoint(sketch, "E19.20.19", {"position": v(-17.62, -30.52) * mm});
            skPoint(sketch, "E19.20.20", {"position": v(-13.38, -32.6) * mm});
            skPoint(sketch, "E19.20.21", {"position": v(-17.62, -30.52) * mm});
            skPoint(sketch, "E19.20.22", {"position": v(-13.38, -32.6) * mm});
            skPoint(sketch, "E19.20.23", {"position": v(-17.62, -30.52) * mm});
            skLineSegment(sketch, "E19.20.24", {"start": v(-13.38, -32.6) * mm, "end": v(-13.28, -32.38) * mm});
            skLineSegment(sketch, "E19.20.25", {"start": v(-17.62, -30.52) * mm, "end": v(-17.5, -30.3) * mm});
            skLineSegment(sketch, "E19.21.0", {"start": v(-11.06, -35.83) * mm, "end": v(-7.2, -36.6) * mm, "construction": true});
            skPoint(sketch, "E19.21.1", {"position": v(-10.89, -33.51) * mm});
            skPoint(sketch, "E19.21.2", {"position": v(-10.66, -32.81) * mm});
            skPoint(sketch, "E19.21.3", {"position": v(-6.17, -33.94) * mm});
            skPoint(sketch, "E19.21.4", {"position": v(-7.2, -36.6) * mm});
            skPoint(sketch, "E19.21.5", {"position": v(-6.3, -34.67) * mm});
            skArc(sketch, "E19.21.6", {"start": v(-10.67, -38.55) * mm, "mid": v(-9.78, -38.79) * mm, "end": v(-8.9, -39) * mm});
            skPoint(sketch, "E19.21.7", {"position": v(-11.06, -35.83) * mm});
            skArc(sketch, "E19.21.8", {"start": v(-5.69, -34.03) * mm, "mid": v(-6.06, -34.11) * mm, "end": v(-6.26, -34.43) * mm});
            skPoint(sketch, "E19.21.9", {"position": v(-10.89, -33.51) * mm});
            skPoint(sketch, "E19.21.10", {"position": v(-6.3, -34.67) * mm});
            skArc(sketch, "E19.21.11", {"start": v(-10.81, -33.28) * mm, "mid": v(-10.84, -32.9) * mm, "end": v(-11.13, -32.66) * mm});
            skPoint(sketch, "E19.21.12", {"position": v(-6.3, -34.67) * mm});
            skPoint(sketch, "E19.21.13", {"position": v(-10.89, -33.51) * mm});
            skPoint(sketch, "E19.21.14", {"position": v(-6.3, -34.67) * mm});
            skPoint(sketch, "E19.21.15", {"position": v(-10.89, -33.51) * mm});
            skPoint(sketch, "E19.21.16", {"position": v(-10.89, -33.51) * mm});
            skPoint(sketch, "E19.21.17", {"position": v(-6.3, -34.67) * mm});
            skPoint(sketch, "E19.21.18", {"position": v(-6.3, -34.67) * mm});
            skPoint(sketch, "E19.21.19", {"position": v(-10.89, -33.51) * mm});
            skPoint(sketch, "E19.21.20", {"position": v(-6.3, -34.67) * mm});
            skPoint(sketch, "E19.21.21", {"position": v(-10.89, -33.51) * mm});
            skPoint(sketch, "E19.21.22", {"position": v(-6.3, -34.67) * mm});
            skPoint(sketch, "E19.21.23", {"position": v(-10.89, -33.51) * mm});
            skLineSegment(sketch, "E19.21.24", {"start": v(-6.3, -34.67) * mm, "end": v(-6.26, -34.43) * mm});
            skLineSegment(sketch, "E19.21.25", {"start": v(-10.89, -33.51) * mm, "end": v(-10.81, -33.28) * mm});
            skLineSegment(sketch, "E19.22.0", {"start": v(-3.36, -37.35) * mm, "end": v(0.56, -37.3) * mm, "construction": true});
            skPoint(sketch, "E19.22.1", {"position": v(-3.68, -35.05) * mm});
            skPoint(sketch, "E19.22.2", {"position": v(-3.6, -34.31) * mm});
            skPoint(sketch, "E19.22.3", {"position": v(1.02, -34.48) * mm});
            skPoint(sketch, "E19.22.4", {"position": v(0.56, -37.3) * mm});
            skPoint(sketch, "E19.22.5", {"position": v(1.04, -35.22) * mm});
            skArc(sketch, "E19.22.6", {"start": v(-2.42, -39.93) * mm, "mid": v(-1.5, -39.97) * mm, "end": v(-0.6, -40) * mm});
            skPoint(sketch, "E19.22.7", {"position": v(-3.36, -37.35) * mm});
            skArc(sketch, "E19.22.8", {"start": v(1.51, -34.47) * mm, "mid": v(1.17, -34.63) * mm, "end": v(1.03, -34.98) * mm});
            skPoint(sketch, "E19.22.9", {"position": v(-3.68, -35.05) * mm});
            skPoint(sketch, "E19.22.10", {"position": v(1.04, -35.22) * mm});
            skArc(sketch, "E19.22.11", {"start": v(-3.66, -34.8) * mm, "mid": v(-3.76, -34.44) * mm, "end": v(-4.1, -34.26) * mm});
            skPoint(sketch, "E19.22.12", {"position": v(1.04, -35.22) * mm});
            skPoint(sketch, "E19.22.13", {"position": v(-3.68, -35.05) * mm});
            skPoint(sketch, "E19.22.14", {"position": v(1.04, -35.22) * mm});
            skPoint(sketch, "E19.22.15", {"position": v(-3.68, -35.05) * mm});
            skPoint(sketch, "E19.22.16", {"position": v(-3.68, -35.05) * mm});
            skPoint(sketch, "E19.22.17", {"position": v(1.04, -35.22) * mm});
            skPoint(sketch, "E19.22.18", {"position": v(1.04, -35.22) * mm});
            skPoint(sketch, "E19.22.19", {"position": v(-3.68, -35.05) * mm});
            skPoint(sketch, "E19.22.20", {"position": v(1.04, -35.22) * mm});
            skPoint(sketch, "E19.22.21", {"position": v(-3.68, -35.05) * mm});
            skPoint(sketch, "E19.22.22", {"position": v(1.04, -35.22) * mm});
            skPoint(sketch, "E19.22.23", {"position": v(-3.68, -35.05) * mm});
            skLineSegment(sketch, "E19.22.24", {"start": v(1.04, -35.22) * mm, "end": v(1.03, -34.98) * mm});
            skLineSegment(sketch, "E19.22.25", {"start": v(-3.68, -35.05) * mm, "end": v(-3.66, -34.8) * mm});
            skLineSegment(sketch, "E19.23.0", {"start": v(4.47, -37.23) * mm, "end": v(8.3, -36.36) * mm, "construction": true});
            skPoint(sketch, "E19.23.1", {"position": v(3.68, -35.05) * mm});
            skPoint(sketch, "E19.23.2", {"position": v(3.6, -34.31) * mm});
            skPoint(sketch, "E19.23.3", {"position": v(8.17, -33.52) * mm});
            skPoint(sketch, "E19.23.4", {"position": v(8.3, -36.36) * mm});
            skPoint(sketch, "E19.23.5", {"position": v(8.34, -34.24) * mm});
            skArc(sketch, "E19.23.6", {"start": v(5.94, -39.56) * mm, "mid": v(6.84, -39.41) * mm, "end": v(7.74, -39.24) * mm});
            skPoint(sketch, "E19.23.7", {"position": v(4.47, -37.23) * mm});
            skArc(sketch, "E19.23.8", {"start": v(8.64, -33.4) * mm, "mid": v(8.34, -33.63) * mm, "end": v(8.28, -34) * mm});
            skPoint(sketch, "E19.23.9", {"position": v(3.68, -35.05) * mm});
            skPoint(sketch, "E19.23.10", {"position": v(8.34, -34.24) * mm});
            skArc(sketch, "E19.23.11", {"start": v(3.66, -34.8) * mm, "mid": v(3.48, -34.47) * mm, "end": v(3.12, -34.36) * mm});
            skPoint(sketch, "E19.23.12", {"position": v(8.34, -34.24) * mm});
            skPoint(sketch, "E19.23.13", {"position": v(3.68, -35.05) * mm});
            skPoint(sketch, "E19.23.14", {"position": v(8.34, -34.24) * mm});
            skPoint(sketch, "E19.23.15", {"position": v(3.68, -35.05) * mm});
            skPoint(sketch, "E19.23.16", {"position": v(3.68, -35.05) * mm});
            skPoint(sketch, "E19.23.17", {"position": v(8.34, -34.24) * mm});
            skPoint(sketch, "E19.23.18", {"position": v(8.34, -34.24) * mm});
            skPoint(sketch, "E19.23.19", {"position": v(3.68, -35.05) * mm});
            skPoint(sketch, "E19.23.20", {"position": v(8.34, -34.24) * mm});
            skPoint(sketch, "E19.23.21", {"position": v(3.68, -35.05) * mm});
            skPoint(sketch, "E19.23.22", {"position": v(8.34, -34.24) * mm});
            skPoint(sketch, "E19.23.23", {"position": v(3.68, -35.05) * mm});
            skLineSegment(sketch, "E19.23.24", {"start": v(8.34, -34.24) * mm, "end": v(8.28, -34) * mm});
            skLineSegment(sketch, "E19.23.25", {"start": v(3.68, -35.05) * mm, "end": v(3.66, -34.8) * mm});
            skLineSegment(sketch, "E19.24.0", {"start": v(12.12, -35.49) * mm, "end": v(15.67, -33.84) * mm, "construction": true});
            skPoint(sketch, "E19.24.1", {"position": v(10.89, -33.51) * mm});
            skPoint(sketch, "E19.24.2", {"position": v(10.66, -32.81) * mm});
            skPoint(sketch, "E19.24.3", {"position": v(14.96, -31.09) * mm});
            skPoint(sketch, "E19.24.4", {"position": v(15.67, -33.84) * mm});
            skPoint(sketch, "E19.24.5", {"position": v(15.28, -31.76) * mm});
            skArc(sketch, "E19.24.6", {"start": v(14.03, -37.46) * mm, "mid": v(14.88, -37.13) * mm, "end": v(15.73, -36.78) * mm});
            skPoint(sketch, "E19.24.7", {"position": v(12.12, -35.49) * mm});
            skArc(sketch, "E19.24.8", {"start": v(15.4, -30.87) * mm, "mid": v(15.15, -31.16) * mm, "end": v(15.17, -31.54) * mm});
            skPoint(sketch, "E19.24.9", {"position": v(10.89, -33.51) * mm});
            skPoint(sketch, "E19.24.10", {"position": v(15.28, -31.76) * mm});
            skArc(sketch, "E19.24.11", {"start": v(10.81, -33.28) * mm, "mid": v(10.57, -33) * mm, "end": v(10.2, -32.96) * mm});
            skPoint(sketch, "E19.24.12", {"position": v(15.28, -31.76) * mm});
            skPoint(sketch, "E19.24.13", {"position": v(10.89, -33.51) * mm});
            skPoint(sketch, "E19.24.14", {"position": v(15.28, -31.76) * mm});
            skPoint(sketch, "E19.24.15", {"position": v(10.89, -33.51) * mm});
            skPoint(sketch, "E19.24.16", {"position": v(10.89, -33.51) * mm});
            skPoint(sketch, "E19.24.17", {"position": v(15.28, -31.76) * mm});
            skPoint(sketch, "E19.24.18", {"position": v(15.28, -31.76) * mm});
            skPoint(sketch, "E19.24.19", {"position": v(10.89, -33.51) * mm});
            skPoint(sketch, "E19.24.20", {"position": v(15.28, -31.76) * mm});
            skPoint(sketch, "E19.24.21", {"position": v(10.89, -33.51) * mm});
            skPoint(sketch, "E19.24.22", {"position": v(15.28, -31.76) * mm});
            skPoint(sketch, "E19.24.23", {"position": v(10.89, -33.51) * mm});
            skLineSegment(sketch, "E19.24.24", {"start": v(15.28, -31.76) * mm, "end": v(15.17, -31.54) * mm});
            skLineSegment(sketch, "E19.24.25", {"start": v(10.89, -33.51) * mm, "end": v(10.81, -33.28) * mm});
            skLineSegment(sketch, "E19.25.0", {"start": v(19.23, -32.2) * mm, "end": v(22.37, -29.84) * mm, "construction": true});
            skPoint(sketch, "E19.25.1", {"position": v(17.62, -30.52) * mm});
            skPoint(sketch, "E19.25.2", {"position": v(17.25, -29.88) * mm});
            skPoint(sketch, "E19.25.3", {"position": v(21.1, -27.3) * mm});
            skPoint(sketch, "E19.25.4", {"position": v(22.37, -29.84) * mm});
            skPoint(sketch, "E19.25.5", {"position": v(21.54, -27.89) * mm});
            skArc(sketch, "E19.25.6", {"start": v(21.51, -33.72) * mm, "mid": v(22.28, -33.22) * mm, "end": v(23.03, -32.7) * mm});
            skPoint(sketch, "E19.25.7", {"position": v(19.23, -32.2) * mm});
            skArc(sketch, "E19.25.8", {"start": v(21.48, -27) * mm, "mid": v(21.3, -27.33) * mm, "end": v(21.4, -27.7) * mm});
            skPoint(sketch, "E19.25.9", {"position": v(17.62, -30.52) * mm});
            skPoint(sketch, "E19.25.10", {"position": v(21.54, -27.89) * mm});
            skArc(sketch, "E19.25.11", {"start": v(17.5, -30.3) * mm, "mid": v(17.2, -30.08) * mm, "end": v(16.82, -30.12) * mm});
            skPoint(sketch, "E19.25.12", {"position": v(21.54, -27.89) * mm});
            skPoint(sketch, "E19.25.13", {"position": v(17.62, -30.52) * mm});
            skPoint(sketch, "E19.25.14", {"position": v(21.54, -27.89) * mm});
            skPoint(sketch, "E19.25.15", {"position": v(17.62, -30.52) * mm});
            skPoint(sketch, "E19.25.16", {"position": v(17.62, -30.52) * mm});
            skPoint(sketch, "E19.25.17", {"position": v(21.54, -27.89) * mm});
            skPoint(sketch, "E19.25.18", {"position": v(21.54, -27.89) * mm});
            skPoint(sketch, "E19.25.19", {"position": v(17.62, -30.52) * mm});
            skPoint(sketch, "E19.25.20", {"position": v(21.54, -27.89) * mm});
            skPoint(sketch, "E19.25.21", {"position": v(17.62, -30.52) * mm});
            skPoint(sketch, "E19.25.22", {"position": v(21.54, -27.89) * mm});
            skPoint(sketch, "E19.25.23", {"position": v(17.62, -30.52) * mm});
            skLineSegment(sketch, "E19.25.24", {"start": v(21.54, -27.89) * mm, "end": v(21.4, -27.7) * mm});
            skLineSegment(sketch, "E19.25.25", {"start": v(17.62, -30.52) * mm, "end": v(17.5, -30.3) * mm});
            skLineSegment(sketch, "E19.26.0", {"start": v(25.5, -27.5) * mm, "end": v(28.08, -24.54) * mm, "construction": true});
            skPoint(sketch, "E19.26.1", {"position": v(23.58, -26.19) * mm});
            skPoint(sketch, "E19.26.2", {"position": v(23.09, -25.64) * mm});
            skPoint(sketch, "E19.26.3", {"position": v(26.3, -22.32) * mm});
            skPoint(sketch, "E19.26.4", {"position": v(28.08, -24.54) * mm});
            skPoint(sketch, "E19.26.5", {"position": v(26.87, -22.8) * mm});
            skArc(sketch, "E19.26.6", {"start": v(28.05, -28.51) * mm, "mid": v(28.7, -27.86) * mm, "end": v(29.33, -27.2) * mm});
            skPoint(sketch, "E19.26.7", {"position": v(25.5, -27.5) * mm});
            skArc(sketch, "E19.26.8", {"start": v(26.62, -21.94) * mm, "mid": v(26.51, -22.3) * mm, "end": v(26.69, -22.64) * mm});
            skPoint(sketch, "E19.26.9", {"position": v(23.58, -26.19) * mm});
            skPoint(sketch, "E19.26.10", {"position": v(26.87, -22.8) * mm});
            skArc(sketch, "E19.26.11", {"start": v(23.42, -26) * mm, "mid": v(23.08, -25.84) * mm, "end": v(22.72, -25.97) * mm});
            skPoint(sketch, "E19.26.12", {"position": v(26.87, -22.8) * mm});
            skPoint(sketch, "E19.26.13", {"position": v(23.58, -26.19) * mm});
            skPoint(sketch, "E19.26.14", {"position": v(26.87, -22.8) * mm});
            skPoint(sketch, "E19.26.15", {"position": v(23.58, -26.19) * mm});
            skPoint(sketch, "E19.26.16", {"position": v(23.58, -26.19) * mm});
            skPoint(sketch, "E19.26.17", {"position": v(26.87, -22.8) * mm});
            skPoint(sketch, "E19.26.18", {"position": v(26.87, -22.8) * mm});
            skPoint(sketch, "E19.26.19", {"position": v(23.58, -26.19) * mm});
            skPoint(sketch, "E19.26.20", {"position": v(26.87, -22.8) * mm});
            skPoint(sketch, "E19.26.21", {"position": v(23.58, -26.19) * mm});
            skPoint(sketch, "E19.26.22", {"position": v(26.87, -22.8) * mm});
            skPoint(sketch, "E19.26.23", {"position": v(23.58, -26.19) * mm});
            skLineSegment(sketch, "E19.26.24", {"start": v(26.87, -22.8) * mm, "end": v(26.69, -22.64) * mm});
            skLineSegment(sketch, "E19.26.25", {"start": v(23.58, -26.19) * mm, "end": v(23.42, -26) * mm});
            skLineSegment(sketch, "E19.27.0", {"start": v(30.66, -21.59) * mm, "end": v(32.57, -18.16) * mm, "construction": true});
            skPoint(sketch, "E19.27.1", {"position": v(28.5, -20.71) * mm});
            skPoint(sketch, "E19.27.2", {"position": v(27.91, -20.28) * mm});
            skPoint(sketch, "E19.27.3", {"position": v(30.37, -16.36) * mm});
            skPoint(sketch, "E19.27.4", {"position": v(32.57, -18.16) * mm});
            skPoint(sketch, "E19.27.5", {"position": v(31.02, -16.71) * mm});
            skArc(sketch, "E19.27.6", {"start": v(33.37, -22.06) * mm, "mid": v(33.86, -21.29) * mm, "end": v(34.34, -20.5) * mm});
            skPoint(sketch, "E19.27.7", {"position": v(30.66, -21.59) * mm});
            skArc(sketch, "E19.27.8", {"start": v(30.6, -15.93) * mm, "mid": v(30.57, -16.3) * mm, "end": v(30.81, -16.6) * mm});
            skPoint(sketch, "E19.27.9", {"position": v(28.5, -20.71) * mm});
            skPoint(sketch, "E19.27.10", {"position": v(31.02, -16.71) * mm});
            skArc(sketch, "E19.27.11", {"start": v(28.31, -20.57) * mm, "mid": v(27.94, -20.48) * mm, "end": v(27.62, -20.68) * mm});
            skPoint(sketch, "E19.27.12", {"position": v(31.02, -16.71) * mm});
            skPoint(sketch, "E19.27.13", {"position": v(28.5, -20.71) * mm});
            skPoint(sketch, "E19.27.14", {"position": v(31.02, -16.71) * mm});
            skPoint(sketch, "E19.27.15", {"position": v(28.5, -20.71) * mm});
            skPoint(sketch, "E19.27.16", {"position": v(28.5, -20.71) * mm});
            skPoint(sketch, "E19.27.17", {"position": v(31.02, -16.71) * mm});
            skPoint(sketch, "E19.27.18", {"position": v(31.02, -16.71) * mm});
            skPoint(sketch, "E19.27.19", {"position": v(28.5, -20.71) * mm});
            skPoint(sketch, "E19.27.20", {"position": v(31.02, -16.71) * mm});
            skPoint(sketch, "E19.27.21", {"position": v(28.5, -20.71) * mm});
            skPoint(sketch, "E19.27.22", {"position": v(31.02, -16.71) * mm});
            skPoint(sketch, "E19.27.23", {"position": v(28.5, -20.71) * mm});
            skLineSegment(sketch, "E19.27.24", {"start": v(31.02, -16.71) * mm, "end": v(30.81, -16.6) * mm});
            skLineSegment(sketch, "E19.27.25", {"start": v(28.5, -20.71) * mm, "end": v(28.31, -20.57) * mm});
            skLineSegment(sketch, "E19.28.0", {"start": v(34.48, -14.74) * mm, "end": v(35.64, -11) * mm, "construction": true});
            skPoint(sketch, "E19.28.1", {"position": v(32.2, -14.33) * mm});
            skPoint(sketch, "E19.28.2", {"position": v(31.52, -14.03) * mm});
            skPoint(sketch, "E19.28.3", {"position": v(33.11, -9.69) * mm});
            skPoint(sketch, "E19.28.4", {"position": v(35.64, -11) * mm});
            skPoint(sketch, "E19.28.5", {"position": v(33.82, -9.9) * mm});
            skArc(sketch, "E19.28.6", {"start": v(37.23, -14.64) * mm, "mid": v(37.55, -13.78) * mm, "end": v(37.86, -12.92) * mm});
            skPoint(sketch, "E19.28.7", {"position": v(34.48, -14.74) * mm});
            skArc(sketch, "E19.28.8", {"start": v(33.25, -9.21) * mm, "mid": v(33.3, -9.6) * mm, "end": v(33.59, -9.83) * mm});
            skPoint(sketch, "E19.28.9", {"position": v(32.2, -14.33) * mm});
            skPoint(sketch, "E19.28.10", {"position": v(33.82, -9.9) * mm});
            skArc(sketch, "E19.28.11", {"start": v(31.97, -14.23) * mm, "mid": v(31.6, -14.22) * mm, "end": v(31.31, -14.48) * mm});
            skPoint(sketch, "E19.28.12", {"position": v(33.82, -9.9) * mm});
            skPoint(sketch, "E19.28.13", {"position": v(32.2, -14.33) * mm});
            skPoint(sketch, "E19.28.14", {"position": v(33.82, -9.9) * mm});
            skPoint(sketch, "E19.28.15", {"position": v(32.2, -14.33) * mm});
            skPoint(sketch, "E19.28.16", {"position": v(32.2, -14.33) * mm});
            skPoint(sketch, "E19.28.17", {"position": v(33.82, -9.9) * mm});
            skPoint(sketch, "E19.28.18", {"position": v(33.82, -9.9) * mm});
            skPoint(sketch, "E19.28.19", {"position": v(32.2, -14.33) * mm});
            skPoint(sketch, "E19.28.20", {"position": v(33.82, -9.9) * mm});
            skPoint(sketch, "E19.28.21", {"position": v(32.2, -14.33) * mm});
            skPoint(sketch, "E19.28.22", {"position": v(33.82, -9.9) * mm});
            skPoint(sketch, "E19.28.23", {"position": v(32.2, -14.33) * mm});
            skLineSegment(sketch, "E19.28.24", {"start": v(33.82, -9.9) * mm, "end": v(33.59, -9.83) * mm});
            skLineSegment(sketch, "E19.28.25", {"start": v(32.2, -14.33) * mm, "end": v(31.97, -14.23) * mm});
            skLineSegment(sketch, "E19.29.0", {"start": v(36.8, -7.25) * mm, "end": v(37.14, -3.35) * mm, "construction": true});
            skPoint(sketch, "E19.29.1", {"position": v(34.47, -7.33) * mm});
            skPoint(sketch, "E19.29.2", {"position": v(33.75, -7.17) * mm});
            skPoint(sketch, "E19.29.3", {"position": v(34.4, -2.6) * mm});
            skPoint(sketch, "E19.29.4", {"position": v(37.14, -3.35) * mm});
            skPoint(sketch, "E19.29.5", {"position": v(35.14, -2.65) * mm});
            skArc(sketch, "E19.29.6", {"start": v(39.46, -6.58) * mm, "mid": v(39.6, -5.67) * mm, "end": v(39.71, -4.77) * mm});
            skPoint(sketch, "E19.29.7", {"position": v(36.8, -7.25) * mm});
            skArc(sketch, "E19.29.8", {"start": v(34.44, -2.1) * mm, "mid": v(34.56, -2.46) * mm, "end": v(34.9, -2.63) * mm});
            skPoint(sketch, "E19.29.9", {"position": v(34.47, -7.33) * mm});
            skPoint(sketch, "E19.29.10", {"position": v(35.14, -2.65) * mm});
            skArc(sketch, "E19.29.11", {"start": v(34.23, -7.28) * mm, "mid": v(33.86, -7.34) * mm, "end": v(33.64, -7.65) * mm});
            skPoint(sketch, "E19.29.12", {"position": v(35.14, -2.65) * mm});
            skPoint(sketch, "E19.29.13", {"position": v(34.47, -7.33) * mm});
            skPoint(sketch, "E19.29.14", {"position": v(35.14, -2.65) * mm});
            skPoint(sketch, "E19.29.15", {"position": v(34.47, -7.33) * mm});
            skPoint(sketch, "E19.29.16", {"position": v(34.47, -7.33) * mm});
            skPoint(sketch, "E19.29.17", {"position": v(35.14, -2.65) * mm});
            skPoint(sketch, "E19.29.18", {"position": v(35.14, -2.65) * mm});
            skPoint(sketch, "E19.29.19", {"position": v(34.47, -7.33) * mm});
            skPoint(sketch, "E19.29.20", {"position": v(35.14, -2.65) * mm});
            skPoint(sketch, "E19.29.21", {"position": v(34.47, -7.33) * mm});
            skPoint(sketch, "E19.29.22", {"position": v(35.14, -2.65) * mm});
            skPoint(sketch, "E19.29.23", {"position": v(34.47, -7.33) * mm});
            skLineSegment(sketch, "E19.29.24", {"start": v(35.14, -2.65) * mm, "end": v(34.9, -2.63) * mm});
            skLineSegment(sketch, "E19.29.25", {"start": v(34.47, -7.33) * mm, "end": v(34.23, -7.28) * mm});
            skLineSegment(sketch, "E20", {"start": v(39.2, 6.8) * mm, "end": v(0, 0) * mm, "construction": true});
            skFitSpline(sketch, "E21.MirrorCS", {"points": [v(34.47, 7.33) * mm, v(34.98, 7.5) * mm, v(36.4, 8.24) * mm, v(38.53, 9.87) * mm, v(41.08, 12.62) * mm, v(43.7, 16.68) * mm, v(45.98, 22.11) * mm, v(47.54, 28.9) * mm, v(47.94, 36.93) * mm], "startDerivative": vector(9.66, 2.82) * mm, "endDerivative": vector(0.66, 45.2) * mm});
            skFitSpline(sketch, "E22.MirrorCS", {"points": [v(33.18, 11.87) * mm, v(33.7, 12) * mm, v(35.3, 12.1) * mm, v(37.97, 11.85) * mm, v(41.59, 10.84) * mm, v(45.94, 8.76) * mm, v(50.74, 5.34) * mm, v(55.63, 0.38) * mm, v(60.2, -6.24) * mm], "startDerivative": vector(9.7, 2.67) * mm, "endDerivative": vector(24.31, -38.12) * mm});
            skArc(sketch, "E23.trimOffspring", {"start": v(32.31, 12.09) * mm, "mid": v(32.02, 12.84) * mm, "end": v(31.71, 13.58) * mm});
            skLineSegment(sketch, "E24.1.0", {"start": v(36.92, 14.8) * mm, "end": v(0, 0) * mm, "construction": true});
            skLineSegment(sketch, "E24.2.0", {"start": v(33.04, 22.16) * mm, "end": v(0, 0) * mm, "construction": true});
            skLineSegment(sketch, "E24.3.0", {"start": v(27.71, 28.54) * mm, "end": v(0, 0) * mm, "construction": true});
            skLineSegment(sketch, "E24.4.0", {"start": v(21.17, 33.68) * mm, "end": v(0, 0) * mm, "construction": true});
            skLineSegment(sketch, "E24.5.0", {"start": v(13.7, 37.34) * mm, "end": v(0, 0) * mm, "construction": true});
            skLineSegment(sketch, "E24.6.0", {"start": v(5.64, 39.38) * mm, "end": v(0, 0) * mm, "construction": true});
            skLineSegment(sketch, "E24.7.0", {"start": v(-2.67, 39.7) * mm, "end": v(0, 0) * mm, "construction": true});
            skLineSegment(sketch, "E24.8.0", {"start": v(-10.86, 38.27) * mm, "end": v(0, 0) * mm, "construction": true});
            skLineSegment(sketch, "E24.9.0", {"start": v(-18.58, 35.17) * mm, "end": v(0, 0) * mm, "construction": true});
            skLineSegment(sketch, "E24.10.0", {"start": v(-25.49, 30.54) * mm, "end": v(0, 0) * mm, "construction": true});
            skLineSegment(sketch, "E24.11.0", {"start": v(-31.28, 24.58) * mm, "end": v(0, 0) * mm, "construction": true});
            skLineSegment(sketch, "E24.12.0", {"start": v(-35.7, 17.54) * mm, "end": v(0, 0) * mm, "construction": true});
            skLineSegment(sketch, "E24.13.0", {"start": v(-38.57, 9.73) * mm, "end": v(0, 0) * mm, "construction": true});
            skLineSegment(sketch, "E24.14.0", {"start": v(-39.75, 1.5) * mm, "end": v(0, 0) * mm, "construction": true});
            skLineSegment(sketch, "E24.15.0", {"start": v(-39.2, -6.8) * mm, "end": v(0, 0) * mm, "construction": true});
            skLineSegment(sketch, "E24.16.0", {"start": v(-36.92, -14.8) * mm, "end": v(0, 0) * mm, "construction": true});
            skLineSegment(sketch, "E24.17.0", {"start": v(-33.04, -22.16) * mm, "end": v(0, 0) * mm, "construction": true});
            skLineSegment(sketch, "E24.18.0", {"start": v(-27.71, -28.54) * mm, "end": v(0, 0) * mm, "construction": true});
            skLineSegment(sketch, "E24.19.0", {"start": v(-21.17, -33.68) * mm, "end": v(0, 0) * mm, "construction": true});
            skLineSegment(sketch, "E24.20.0", {"start": v(-13.7, -37.34) * mm, "end": v(0, 0) * mm, "construction": true});
            skLineSegment(sketch, "E24.21.0", {"start": v(-5.64, -39.38) * mm, "end": v(0, 0) * mm, "construction": true});
            skLineSegment(sketch, "E24.22.0", {"start": v(2.67, -39.7) * mm, "end": v(0, 0) * mm, "construction": true});
            skLineSegment(sketch, "E24.23.0", {"start": v(10.86, -38.27) * mm, "end": v(0, 0) * mm, "construction": true});
            skLineSegment(sketch, "E24.24.0", {"start": v(18.58, -35.17) * mm, "end": v(0, 0) * mm, "construction": true});
            skLineSegment(sketch, "E24.25.0", {"start": v(25.49, -30.54) * mm, "end": v(0, 0) * mm, "construction": true});
            skLineSegment(sketch, "E24.26.0", {"start": v(31.28, -24.58) * mm, "end": v(0, 0) * mm, "construction": true});
            skLineSegment(sketch, "E24.27.0", {"start": v(35.7, -17.54) * mm, "end": v(0, 0) * mm, "construction": true});
            skLineSegment(sketch, "E24.28.0", {"start": v(38.57, -9.73) * mm, "end": v(0, 0) * mm, "construction": true});
            skLineSegment(sketch, "E24.29.0", {"start": v(39.75, -1.5) * mm, "end": v(0, 0) * mm, "construction": true});
            skFitSpline(sketch, "E25.MirrorCS", {"points": [v(25.48, 24.34) * mm, v(25.9, 24.66) * mm, v(27.33, 25.42) * mm, v(29.87, 26.27) * mm, v(33.58, 26.82) * mm, v(38.4, 26.7) * mm, v(44.18, 25.52) * mm, v(50.67, 22.97) * mm, v(57.53, 18.78) * mm], "startDerivative": vector(7.78, 6.39) * mm, "endDerivative": vector(37.71, -24.94) * mm});
            skFitSpline(sketch, "E26.MirrorCS", {"points": [v(28.5, 20.71) * mm, v(28.9, 21.08) * mm, v(29.9, 22.34) * mm, v(31.19, 24.69) * mm, v(32.4, 28.24) * mm, v(33.13, 33) * mm, v(33.01, 38.9) * mm, v(31.67, 45.74) * mm, v(28.77, 53.24) * mm], "startDerivative": vector(7.68, 6.5) * mm, "endDerivative": vector(-17.78, 41.57) * mm});
            skFitSpline(sketch, "E27.MirrorCS", {"points": [v(29.98, 18.51) * mm, v(30.47, 18.74) * mm, v(32.02, 19.19) * mm, v(34.68, 19.48) * mm, v(38.42, 19.25) * mm, v(43.11, 18.12) * mm, v(48.52, 15.78) * mm, v(54.34, 11.94) * mm, v(60.18, 6.4) * mm], "startDerivative": vector(8.94, 4.63) * mm, "endDerivative": vector(31.7, -32.23) * mm});
            skFitSpline(sketch, "E28.MirrorCS", {"points": [v(32.2, 14.33) * mm, v(32.65, 14.6) * mm, v(33.9, 15.63) * mm, v(35.64, 17.66) * mm, v(37.56, 20.89) * mm, v(39.27, 25.4) * mm, v(40.38, 31.19) * mm, v(40.49, 38.16) * mm, v(39.21, 46.1) * mm], "startDerivative": vector(8.86, 4.77) * mm, "endDerivative": vector(-8.75, 44.36) * mm});
            skFitSpline(sketch, "E29.MirrorCS", {"points": [v(-1.04, 35.22) * mm, v(-1, 35.76) * mm, v(-0.6, 37.32) * mm, v(0.47, 39.77) * mm, v(2.54, 42.9) * mm, v(5.86, 46.4) * mm, v(10.6, 49.91) * mm, v(16.83, 53.03) * mm, v(24.54, 55.32) * mm], "startDerivative": vector(0.46, 10.05) * mm, "endDerivative": vector(43.77, 11.34) * mm});
            skFitSpline(sketch, "E30.MirrorCS", {"points": [v(3.68, 35.05) * mm, v(3.68, 35.58) * mm, v(3.4, 37.17) * mm, v(2.52, 39.7) * mm, v(0.69, 42.97) * mm, v(-2.36, 46.7) * mm, v(-6.82, 50.57) * mm, v(-12.8, 54.14) * mm, v(-20.31, 57) * mm], "startDerivative": vector(0.3, 10.06) * mm, "endDerivative": vector(-42.8, 14.6) * mm});
            skFitSpline(sketch, "E31.MirrorCS", {"points": [v(6.3, 34.67) * mm, v(6.46, 35.18) * mm, v(7.17, 36.63) * mm, v(8.73, 38.8) * mm, v(11.4, 41.43) * mm, v(15.38, 44.17) * mm, v(20.74, 46.62) * mm, v(27.49, 48.37) * mm, v(35.5, 49) * mm], "startDerivative": vector(2.54, 9.74) * mm, "endDerivative": vector(45.17, 2) * mm});
            skFitSpline(sketch, "E32.MirrorCS", {"points": [v(10.89, 33.51) * mm, v(11, 34.04) * mm, v(11.06, 35.65) * mm, v(10.72, 38.3) * mm, v(9.6, 41.89) * mm, v(7.4, 46.18) * mm, v(3.84, 50.88) * mm, v(-1.26, 55.62) * mm, v(-8.02, 59.98) * mm], "startDerivative": vector(2.39, 9.78) * mm, "endDerivative": vector(-38.82, 23.18) * mm});
            skFitSpline(sketch, "E33.MirrorCS", {"points": [v(13.38, 32.6) * mm, v(13.64, 33.07) * mm, v(14.62, 34.34) * mm, v(16.6, 36.14) * mm, v(19.77, 38.16) * mm, v(24.23, 40) * mm, v(29.98, 41.28) * mm, v(36.94, 41.6) * mm, v(44.92, 40.56) * mm], "startDerivative": vector(4.5, 9) * mm, "endDerivative": vector(44.6, -7.44) * mm});
            skFitSpline(sketch, "E34.MirrorCS", {"points": [v(17.62, 30.52) * mm, v(17.83, 31) * mm, v(18.23, 32.57) * mm, v(18.45, 35.24) * mm, v(18.1, 38.97) * mm, v(16.84, 43.63) * mm, v(14.34, 48.97) * mm, v(10.33, 54.67) * mm, v(4.63, 60.34) * mm], "startDerivative": vector(4.37, 9.07) * mm, "endDerivative": vector(-33.15, 30.74) * mm});
            skFitSpline(sketch, "E35.MirrorCS", {"points": [v(19.86, 29.1) * mm, v(20.21, 29.51) * mm, v(21.44, 30.55) * mm, v(23.76, 31.9) * mm, v(27.27, 33.21) * mm, v(32.02, 34.1) * mm, v(37.91, 34.15) * mm, v(44.79, 33) * mm, v(52.37, 30.33) * mm], "startDerivative": vector(6.28, 7.87) * mm, "endDerivative": vector(42.07, -16.55) * mm});
            skFitSpline(sketch, "E36.MirrorCS", {"points": [v(23.58, 26.19) * mm, v(23.89, 26.62) * mm, v(24.6, 28.06) * mm, v(25.37, 30.63) * mm, v(25.81, 34.36) * mm, v(25.55, 39.18) * mm, v(24.2, 44.92) * mm, v(21.47, 51.32) * mm, v(17.08, 58.06) * mm], "startDerivative": vector(6.16, 7.96) * mm, "endDerivative": vector(-26.04, 36.96) * mm});
            skFitSpline(sketch, "E37.MirrorCS", {"points": [v(-34.92, -4.72) * mm, v(-35.46, -4.73) * mm, v(-37.05, -4.5) * mm, v(-39.6, -3.7) * mm, v(-42.93, -1.96) * mm, v(-46.76, 0.98) * mm, v(-50.74, 5.32) * mm, v(-54.5, 11.2) * mm, v(-57.58, 18.62) * mm], "startDerivative": vector(-10.05, -0.6) * mm, "endDerivative": vector(-15.85, 42.34) * mm});
            skFitSpline(sketch, "E38.MirrorCS", {"points": [v(-35.24, 0) * mm, v(-35.77, -0.06) * mm, v(-37.32, -0.5) * mm, v(-39.74, -1.64) * mm, v(-42.8, -3.8) * mm, v(-46.2, -7.23) * mm, v(-49.58, -12.07) * mm, v(-52.5, -18.39) * mm, v(-54.57, -26.16) * mm], "startDerivative": vector(-10.04, -0.75) * mm, "endDerivative": vector(-10.04, -44.08) * mm});
            skFitSpline(sketch, "E39.MirrorCS", {"points": [v(-35.14, 2.65) * mm, v(-35.67, 2.75) * mm, v(-37.18, 3.3) * mm, v(-39.5, 4.62) * mm, v(-42.4, 7.01) * mm, v(-45.53, 10.68) * mm, v(-48.53, 15.76) * mm, v(-50.98, 22.28) * mm, v(-52.45, 30.19) * mm], "startDerivative": vector(-9.95, 1.5) * mm, "endDerivative": vector(-6.7, 44.71) * mm});
            skFitSpline(sketch, "E40.MirrorCS", {"points": [v(-34.47, 7.33) * mm, v(-35, 7.38) * mm, v(-36.6, 7.28) * mm, v(-39.22, 6.66) * mm, v(-42.66, 5.18) * mm, v(-46.7, 2.54) * mm, v(-51, -1.5) * mm, v(-55.18, -7.07) * mm, v(-58.82, -14.24) * mm], "startDerivative": vector(-9.97, 1.35) * mm, "endDerivative": vector(-19, -41.03) * mm});
            skFitSpline(sketch, "E41.MirrorCS", {"points": [v(-33.82, 9.9) * mm, v(-34.31, 10.1) * mm, v(-35.68, 10.95) * mm, v(-37.68, 12.74) * mm, v(-40.02, 15.67) * mm, v(-42.32, 19.91) * mm, v(-44.2, 25.5) * mm, v(-45.23, 32.4) * mm, v(-45.03, 40.43) * mm], "startDerivative": vector(-9.42, 3.54) * mm, "endDerivative": vector(2.74, 45.13) * mm});
            skFitSpline(sketch, "E42.MirrorCS", {"points": [v(-32.2, 14.33) * mm, v(-32.7, 14.5) * mm, v(-34.3, 14.73) * mm, v(-36.97, 14.67) * mm, v(-40.65, 13.93) * mm, v(-45.15, 12.2) * mm, v(-50.2, 9.14) * mm, v(-55.45, 4.56) * mm, v(-60.5, -1.7) * mm], "startDerivative": vector(-9.47, 3.4) * mm, "endDerivative": vector(-27.1, -36.19) * mm});
            skPoint(sketch, "E43.MirrorP", {"position": v(-32.75, 18.27) * mm});
            skFitSpline(sketch, "E44.MirrorCS", {"points": [v(-28.5, 20.71) * mm, v(-28.98, 20.98) * mm, v(-30.48, 21.54) * mm, v(-33.12, 22.03) * mm, v(-36.87, 22.08) * mm, v(-41.63, 21.31) * mm, v(-47.2, 19.38) * mm, v(-53.29, 15.98) * mm, v(-59.53, 10.91) * mm], "startDerivative": vector(-8.56, 5.3) * mm, "endDerivative": vector(-34.04, -29.76) * mm});
            skFitSpline(sketch, "E45.MirrorCS", {"points": [v(-26.87, 22.8) * mm, v(-27.24, 23.19) * mm, v(-28.14, 24.52) * mm, v(-29.24, 26.96) * mm, v(-30.18, 30.6) * mm, v(-30.56, 35.4) * mm, v(-30, 41.27) * mm, v(-28.14, 47.99) * mm, v(-24.7, 55.25) * mm], "startDerivative": vector(-7.17, 7.07) * mm, "endDerivative": vector(20.86, 40.11) * mm});
            skFitSpline(sketch, "E46.MirrorCS", {"points": [v(-23.58, 26.19) * mm, v(-23.98, 26.54) * mm, v(-25.34, 27.4) * mm, v(-27.81, 28.44) * mm, v(-31.47, 29.26) * mm, v(-36.3, 29.5) * mm, v(-42.14, 28.77) * mm, v(-48.8, 26.71) * mm, v(-55.96, 23.05) * mm], "startDerivative": vector(-7.27, 6.96) * mm, "endDerivative": vector(-39.48, -22.03) * mm});
            skFitSpline(sketch, "E47.MirrorCS", {"points": [v(-21.54, 27.89) * mm, v(-21.82, 28.34) * mm, v(-22.43, 29.83) * mm, v(-23, 32.45) * mm, v(-23.16, 36.2) * mm, v(-22.53, 40.98) * mm, v(-20.76, 46.6) * mm, v(-17.55, 52.8) * mm, v(-12.66, 59.18) * mm], "startDerivative": vector(-5.54, 8.4) * mm, "endDerivative": vector(28.74, 34.9) * mm});
            skFitSpline(sketch, "E48.MirrorCS", {"points": [v(-17.62, 30.52) * mm, v(-17.94, 30.95) * mm, v(-19.09, 32.07) * mm, v(-21.3, 33.6) * mm, v(-24.7, 35.17) * mm, v(-29.36, 36.4) * mm, v(-35.24, 36.9) * mm, v(-42.18, 36.28) * mm, v(-49.94, 34.18) * mm], "startDerivative": vector(-5.67, 8.32) * mm, "endDerivative": vector(-43.2, -13.34) * mm});
            skFitSpline(sketch, "E49.MirrorCS", {"points": [v(-15.28, 31.76) * mm, v(-15.45, 32.26) * mm, v(-15.73, 33.85) * mm, v(-15.75, 36.53) * mm, v(-15.13, 40.23) * mm, v(-13.52, 44.77) * mm, v(-10.62, 49.9) * mm, v(-6.2, 55.29) * mm, v(-0.08, 60.52) * mm], "startDerivative": vector(-3.67, 9.37) * mm, "endDerivative": vector(35.37, 28.16) * mm});
            skFitSpline(sketch, "E50.MirrorCS", {"points": [v(-10.89, 33.51) * mm, v(-11.11, 34) * mm, v(-12, 35.34) * mm, v(-13.84, 37.3) * mm, v(-16.85, 39.54) * mm, v(-21.15, 41.71) * mm, v(-26.8, 43.42) * mm, v(-33.71, 44.25) * mm, v(-41.74, 43.82) * mm], "startDerivative": vector(-3.82, 9.31) * mm, "endDerivative": vector(-45.03, -4.07) * mm});
            skFitSpline(sketch, "E51.MirrorCS", {"points": [v(-8.34, 34.24) * mm, v(-8.4, 34.77) * mm, v(-8.35, 36.38) * mm, v(-7.81, 39) * mm, v(-6.43, 42.5) * mm, v(-3.91, 46.6) * mm, v(0, 51.02) * mm, v(5.44, 55.37) * mm, v(12.5, 59.21) * mm], "startDerivative": vector(-1.65, 9.93) * mm, "endDerivative": vector(40.45, 20.2) * mm});
            skFitSpline(sketch, "E52.MirrorCS", {"points": [v(-3.68, 35.05) * mm, v(-3.8, 35.57) * mm, v(-4.4, 37.06) * mm, v(-5.79, 39.35) * mm, v(-8.26, 42.17) * mm, v(-12.02, 45.2) * mm, v(-17.18, 48.04) * mm, v(-23.78, 50.3) * mm, v(-31.72, 51.54) * mm], "startDerivative": vector(-1.8, 9.9) * mm, "endDerivative": vector(-44.9, 5.38) * mm});
            skFitSpline(sketch, "E53.MirrorCS", {"points": [v(8.34, -34.24) * mm, v(8.4, -34.77) * mm, v(8.35, -36.38) * mm, v(7.81, -39) * mm, v(6.43, -42.5) * mm, v(3.91, -46.6) * mm, v(0, -51.02) * mm, v(-5.44, -55.37) * mm, v(-12.5, -59.21) * mm], "startDerivative": vector(1.65, -9.93) * mm, "endDerivative": vector(-40.45, -20.2) * mm});
            skFitSpline(sketch, "E54.MirrorCS", {"points": [v(3.68, -35.05) * mm, v(3.8, -35.57) * mm, v(4.4, -37.06) * mm, v(5.79, -39.35) * mm, v(8.26, -42.17) * mm, v(12.02, -45.2) * mm, v(17.18, -48.04) * mm, v(23.78, -50.3) * mm, v(31.72, -51.54) * mm], "startDerivative": vector(1.8, -9.9) * mm, "endDerivative": vector(44.9, -5.38) * mm});
            skFitSpline(sketch, "E55.MirrorCS", {"points": [v(1.04, -35.22) * mm, v(1, -35.76) * mm, v(0.6, -37.32) * mm, v(-0.47, -39.77) * mm, v(-2.54, -42.9) * mm, v(-5.86, -46.4) * mm, v(-10.6, -49.91) * mm, v(-16.83, -53.03) * mm, v(-24.54, -55.32) * mm], "startDerivative": vector(-0.46, -10.05) * mm, "endDerivative": vector(-43.77, -11.34) * mm});
            skFitSpline(sketch, "E56.MirrorCS", {"points": [v(-3.68, -35.05) * mm, v(-3.68, -35.58) * mm, v(-3.4, -37.17) * mm, v(-2.52, -39.7) * mm, v(-0.69, -42.97) * mm, v(2.36, -46.7) * mm, v(6.82, -50.57) * mm, v(12.8, -54.14) * mm, v(20.31, -57) * mm], "startDerivative": vector(-0.3, -10.06) * mm, "endDerivative": vector(42.8, -14.6) * mm});
            skFitSpline(sketch, "E57.MirrorCS", {"points": [v(-6.3, -34.67) * mm, v(-6.46, -35.18) * mm, v(-7.17, -36.63) * mm, v(-8.73, -38.8) * mm, v(-11.4, -41.43) * mm, v(-15.38, -44.17) * mm, v(-20.74, -46.62) * mm, v(-27.49, -48.37) * mm, v(-35.5, -49) * mm], "startDerivative": vector(-2.54, -9.74) * mm, "endDerivative": vector(-45.17, -2) * mm});
            skFitSpline(sketch, "E58.MirrorCS", {"points": [v(-10.89, -33.51) * mm, v(-11, -34.04) * mm, v(-11.06, -35.65) * mm, v(-10.72, -38.3) * mm, v(-9.6, -41.89) * mm, v(-7.4, -46.18) * mm, v(-3.84, -50.88) * mm, v(1.26, -55.62) * mm, v(8.02, -59.98) * mm], "startDerivative": vector(-2.39, -9.78) * mm, "endDerivative": vector(38.82, -23.18) * mm});
            skFitSpline(sketch, "E59.MirrorCS", {"points": [v(-13.38, -32.6) * mm, v(-13.64, -33.07) * mm, v(-14.62, -34.34) * mm, v(-16.6, -36.14) * mm, v(-19.77, -38.16) * mm, v(-24.23, -40) * mm, v(-29.98, -41.28) * mm, v(-36.94, -41.6) * mm, v(-44.92, -40.56) * mm], "startDerivative": vector(-4.5, -9) * mm, "endDerivative": vector(-44.6, 7.44) * mm});
            skFitSpline(sketch, "E60.MirrorCS", {"points": [v(-17.62, -30.52) * mm, v(-17.83, -31) * mm, v(-18.23, -32.57) * mm, v(-18.45, -35.24) * mm, v(-18.1, -38.97) * mm, v(-16.84, -43.63) * mm, v(-14.34, -48.97) * mm, v(-10.33, -54.67) * mm, v(-4.63, -60.34) * mm], "startDerivative": vector(-4.37, -9.07) * mm, "endDerivative": vector(33.15, -30.74) * mm});
            skFitSpline(sketch, "E61.MirrorCS", {"points": [v(-19.86, -29.1) * mm, v(-20.21, -29.51) * mm, v(-21.44, -30.55) * mm, v(-23.76, -31.9) * mm, v(-27.27, -33.21) * mm, v(-32.02, -34.1) * mm, v(-37.91, -34.15) * mm, v(-44.79, -33) * mm, v(-52.37, -30.33) * mm], "startDerivative": vector(-6.28, -7.87) * mm, "endDerivative": vector(-42.07, 16.55) * mm});
            skFitSpline(sketch, "E62.MirrorCS", {"points": [v(-25.48, -24.34) * mm, v(-25.9, -24.66) * mm, v(-27.33, -25.42) * mm, v(-29.87, -26.27) * mm, v(-33.58, -26.82) * mm, v(-38.4, -26.7) * mm, v(-44.18, -25.52) * mm, v(-50.67, -22.97) * mm, v(-57.53, -18.78) * mm], "startDerivative": vector(-7.78, -6.39) * mm, "endDerivative": vector(-37.71, 24.94) * mm});
            skFitSpline(sketch, "E63.MirrorCS", {"points": [v(-28.5, -20.71) * mm, v(-28.9, -21.08) * mm, v(-29.9, -22.34) * mm, v(-31.19, -24.69) * mm, v(-32.4, -28.24) * mm, v(-33.13, -33) * mm, v(-33.01, -38.9) * mm, v(-31.67, -45.74) * mm, v(-28.77, -53.24) * mm], "startDerivative": vector(-7.68, -6.5) * mm, "endDerivative": vector(17.78, -41.57) * mm});
            skFitSpline(sketch, "E64.MirrorCS", {"points": [v(-29.98, -18.51) * mm, v(-30.47, -18.74) * mm, v(-32.02, -19.19) * mm, v(-34.68, -19.48) * mm, v(-38.42, -19.25) * mm, v(-43.11, -18.12) * mm, v(-48.52, -15.78) * mm, v(-54.34, -11.94) * mm, v(-60.18, -6.4) * mm], "startDerivative": vector(-8.94, -4.63) * mm, "endDerivative": vector(-31.7, 32.23) * mm});
            skFitSpline(sketch, "E65.MirrorCS", {"points": [v(-32.2, -14.33) * mm, v(-32.65, -14.6) * mm, v(-33.9, -15.63) * mm, v(-35.64, -17.66) * mm, v(-37.56, -20.89) * mm, v(-39.27, -25.4) * mm, v(-40.38, -31.19) * mm, v(-40.49, -38.16) * mm, v(-39.21, -46.1) * mm], "startDerivative": vector(-8.86, -4.77) * mm, "endDerivative": vector(8.75, -44.36) * mm});
            skFitSpline(sketch, "E66.MirrorCS", {"points": [v(-33.18, -11.87) * mm, v(-33.7, -12) * mm, v(-35.3, -12.1) * mm, v(-37.97, -11.85) * mm, v(-41.59, -10.84) * mm, v(-45.94, -8.76) * mm, v(-50.74, -5.34) * mm, v(-55.63, -0.38) * mm, v(-60.2, 6.24) * mm], "startDerivative": vector(-9.7, -2.67) * mm, "endDerivative": vector(-24.31, 38.12) * mm});
            skFitSpline(sketch, "E67.MirrorCS", {"points": [v(-34.47, -7.33) * mm, v(-34.98, -7.5) * mm, v(-36.4, -8.24) * mm, v(-38.53, -9.87) * mm, v(-41.08, -12.62) * mm, v(-43.7, -16.68) * mm, v(-45.98, -22.11) * mm, v(-47.54, -28.9) * mm, v(-47.94, -36.93) * mm], "startDerivative": vector(-9.66, -2.82) * mm, "endDerivative": vector(-0.66, -45.2) * mm});
            skFitSpline(sketch, "E68.MirrorCS", {"points": [v(-31.02, 16.71) * mm, v(-31.46, 17.02) * mm, v(-32.62, 18.13) * mm, v(-34.21, 20.3) * mm, v(-35.88, 23.65) * mm, v(-37.25, 28.28) * mm, v(-37.92, 34.13) * mm, v(-37.5, 41.1) * mm, v(-35.64, 48.91) * mm], "startDerivative": vector(-8.48, 5.42) * mm, "endDerivative": vector(12.06, 43.57) * mm});
            skFitSpline(sketch, "E69.MirrorCS", {"points": [v(-23.58, -26.19) * mm, v(-23.89, -26.62) * mm, v(-24.6, -28.06) * mm, v(-25.37, -30.63) * mm, v(-25.81, -34.36) * mm, v(-25.55, -39.18) * mm, v(-24.2, -44.92) * mm, v(-21.47, -51.32) * mm, v(-17.08, -58.06) * mm], "startDerivative": vector(-6.16, -7.96) * mm, "endDerivative": vector(26.04, -36.96) * mm});
            skFitSpline(sketch, "E70.MirrorCS", {"points": [v(35.14, -2.65) * mm, v(35.67, -2.75) * mm, v(37.18, -3.3) * mm, v(39.5, -4.62) * mm, v(42.4, -7.01) * mm, v(45.53, -10.68) * mm, v(48.53, -15.76) * mm, v(50.98, -22.28) * mm, v(52.45, -30.19) * mm], "startDerivative": vector(9.95, -1.5) * mm, "endDerivative": vector(6.7, -44.71) * mm});
            skFitSpline(sketch, "E71.MirrorCS", {"points": [v(34.47, -7.33) * mm, v(35, -7.38) * mm, v(36.6, -7.28) * mm, v(39.22, -6.66) * mm, v(42.66, -5.18) * mm, v(46.7, -2.54) * mm, v(51, 1.5) * mm, v(55.18, 7.07) * mm, v(58.82, 14.24) * mm], "startDerivative": vector(9.97, -1.35) * mm, "endDerivative": vector(19, 41.03) * mm});
            skFitSpline(sketch, "E72.MirrorCS", {"points": [v(33.82, -9.9) * mm, v(34.31, -10.1) * mm, v(35.68, -10.95) * mm, v(37.68, -12.74) * mm, v(40.02, -15.67) * mm, v(42.32, -19.91) * mm, v(44.2, -25.5) * mm, v(45.23, -32.4) * mm, v(45.03, -40.43) * mm], "startDerivative": vector(9.42, -3.54) * mm, "endDerivative": vector(-2.74, -45.13) * mm});
            skFitSpline(sketch, "E73.MirrorCS", {"points": [v(32.2, -14.33) * mm, v(32.7, -14.5) * mm, v(34.3, -14.73) * mm, v(36.97, -14.67) * mm, v(40.65, -13.93) * mm, v(45.15, -12.2) * mm, v(50.2, -9.14) * mm, v(55.45, -4.56) * mm, v(60.5, 1.7) * mm], "startDerivative": vector(9.47, -3.4) * mm, "endDerivative": vector(27.1, 36.19) * mm});
            skFitSpline(sketch, "E74.MirrorCS", {"points": [v(31.02, -16.71) * mm, v(31.46, -17.02) * mm, v(32.62, -18.13) * mm, v(34.21, -20.3) * mm, v(35.88, -23.65) * mm, v(37.25, -28.28) * mm, v(37.92, -34.13) * mm, v(37.5, -41.1) * mm, v(35.64, -48.91) * mm], "startDerivative": vector(8.48, -5.42) * mm, "endDerivative": vector(-12.06, -43.57) * mm});
            skFitSpline(sketch, "E75.MirrorCS", {"points": [v(28.5, -20.71) * mm, v(28.98, -20.98) * mm, v(30.48, -21.54) * mm, v(33.12, -22.03) * mm, v(36.87, -22.08) * mm, v(41.63, -21.31) * mm, v(47.2, -19.38) * mm, v(53.29, -15.98) * mm, v(59.53, -10.91) * mm], "startDerivative": vector(8.56, -5.3) * mm, "endDerivative": vector(34.04, 29.76) * mm});
            skFitSpline(sketch, "E76.MirrorCS", {"points": [v(26.87, -22.8) * mm, v(27.24, -23.19) * mm, v(28.14, -24.52) * mm, v(29.24, -26.96) * mm, v(30.18, -30.6) * mm, v(30.56, -35.4) * mm, v(30, -41.27) * mm, v(28.14, -47.99) * mm, v(24.7, -55.25) * mm], "startDerivative": vector(7.17, -7.07) * mm, "endDerivative": vector(-20.86, -40.11) * mm});
            skFitSpline(sketch, "E77.MirrorCS", {"points": [v(23.58, -26.19) * mm, v(23.98, -26.54) * mm, v(25.34, -27.4) * mm, v(27.81, -28.44) * mm, v(31.47, -29.26) * mm, v(36.3, -29.5) * mm, v(42.14, -28.77) * mm, v(48.8, -26.71) * mm, v(55.96, -23.05) * mm], "startDerivative": vector(7.27, -6.96) * mm, "endDerivative": vector(39.48, 22.03) * mm});
            skFitSpline(sketch, "E78.MirrorCS", {"points": [v(21.54, -27.89) * mm, v(21.82, -28.34) * mm, v(22.43, -29.83) * mm, v(23, -32.45) * mm, v(23.16, -36.2) * mm, v(22.53, -40.98) * mm, v(20.76, -46.6) * mm, v(17.55, -52.8) * mm, v(12.66, -59.18) * mm], "startDerivative": vector(5.54, -8.4) * mm, "endDerivative": vector(-28.74, -34.9) * mm});
            skFitSpline(sketch, "E79.MirrorCS", {"points": [v(17.62, -30.52) * mm, v(17.94, -30.95) * mm, v(19.09, -32.07) * mm, v(21.3, -33.6) * mm, v(24.7, -35.17) * mm, v(29.36, -36.4) * mm, v(35.24, -36.9) * mm, v(42.18, -36.28) * mm, v(49.94, -34.18) * mm], "startDerivative": vector(5.67, -8.32) * mm, "endDerivative": vector(43.2, 13.34) * mm});
            skFitSpline(sketch, "E80.MirrorCS", {"points": [v(15.28, -31.76) * mm, v(15.45, -32.26) * mm, v(15.73, -33.85) * mm, v(15.75, -36.53) * mm, v(15.13, -40.23) * mm, v(13.52, -44.77) * mm, v(10.62, -49.9) * mm, v(6.2, -55.29) * mm, v(0.08, -60.52) * mm], "startDerivative": vector(3.67, -9.37) * mm, "endDerivative": vector(-35.37, -28.16) * mm});
            skFitSpline(sketch, "E81.MirrorCS", {"points": [v(10.89, -33.51) * mm, v(11.11, -34) * mm, v(12, -35.34) * mm, v(13.84, -37.3) * mm, v(16.85, -39.54) * mm, v(21.15, -41.71) * mm, v(26.8, -43.42) * mm, v(33.71, -44.25) * mm, v(41.74, -43.82) * mm], "startDerivative": vector(3.82, -9.31) * mm, "endDerivative": vector(45.03, 4.07) * mm});
            skArc(sketch, "E82.trimOffspring", {"start": v(29.1, 18.54) * mm, "mid": v(28.65, 19.21) * mm, "end": v(28.2, 19.88) * mm});
            skArc(sketch, "E83.trimOffspring", {"start": v(27.91, 20.28) * mm, "mid": v(-32.89, -10.43) * mm, "end": v(34.5, -0.5) * mm});
            skSolve(sketch);
        }
        {
            var Q0;
            Q0 = qSketchRegion(id + "F0", true);
            extrude(context, id + "F1", {"entities" : qUnion([Q0]), "depth" : 25 * mm, "offsetDistance" : 25 * mm});
        }
        {
            var Q0;
            Q0=makeQuery(id+"F1.opExtrude","CAP_FACE",FACE,{"disambiguationData":[OSD([sQuery(id+"F0.wireOp",EDGE,"E5"),sQuery(id+"F0.wireOp",EDGE,"E6"),sQuery(id+"F0.wireOp",EDGE,"E7"),sQuery(id+"F0.wireOp",EDGE,"E14.MirrorCS"),sQuery(id+"F0.wireOp",EDGE,"E15"),sQuery(id+"F0.wireOp",EDGE,"E16.MirrorCS"),sQuery(id+"F0.wireOp",EDGE,"E17.filletArc"),sQuery(id+"F0.wireOp",EDGE,"E18.filletArc"),sQuery(id+"F0.wireOp",EDGE,"E19.1.6"),sQuery(id+"F0.wireOp",EDGE,"E19.1.8"),sQuery(id+"F0.wireOp",EDGE,"E19.1.11"),sQuery(id+"F0.wireOp",EDGE,"E19.1.24"),sQuery(id+"F0.wireOp",EDGE,"E19.1.25"),sQuery(id+"F0.wireOp",EDGE,"E19.2.6"),sQuery(id+"F0.wireOp",EDGE,"E19.2.8"),sQuery(id+"F0.wireOp",EDGE,"E19.2.11"),sQuery(id+"F0.wireOp",EDGE,"E19.2.24"),sQuery(id+"F0.wireOp",EDGE,"E19.2.25"),sQuery(id+"F0.wireOp",EDGE,"E19.3.6"),sQuery(id+"F0.wireOp",EDGE,"E19.3.8"),sQuery(id+"F0.wireOp",EDGE,"E19.3.11"),sQuery(id+"F0.wireOp",EDGE,"E19.3.24"),sQuery(id+"F0.wireOp",EDGE,"E19.3.25"),sQuery(id+"F0.wireOp",EDGE,"E19.4.6"),sQuery(id+"F0.wireOp",EDGE,"E19.4.8"),sQuery(id+"F0.wireOp",EDGE,"E19.4.11"),sQuery(id+"F0.wireOp",EDGE,"E19.4.24"),sQuery(id+"F0.wireOp",EDGE,"E19.4.25"),sQuery(id+"F0.wireOp",EDGE,"E19.5.6"),sQuery(id+"F0.wireOp",EDGE,"E19.5.8"),sQuery(id+"F0.wireOp",EDGE,"E19.5.11"),sQuery(id+"F0.wireOp",EDGE,"E19.5.24"),sQuery(id+"F0.wireOp",EDGE,"E19.5.25"),sQuery(id+"F0.wireOp",EDGE,"E19.6.6"),sQuery(id+"F0.wireOp",EDGE,"E19.6.8"),sQuery(id+"F0.wireOp",EDGE,"E19.6.11"),sQuery(id+"F0.wireOp",EDGE,"E19.6.24"),sQuery(id+"F0.wireOp",EDGE,"E19.6.25"),sQuery(id+"F0.wireOp",EDGE,"E19.7.6"),sQuery(id+"F0.wireOp",EDGE,"E19.7.8"),sQuery(id+"F0.wireOp",EDGE,"E19.7.11"),sQuery(id+"F0.wireOp",EDGE,"E19.7.24"),sQuery(id+"F0.wireOp",EDGE,"E19.7.25"),sQuery(id+"F0.wireOp",EDGE,"E19.8.6"),sQuery(id+"F0.wireOp",EDGE,"E19.8.8"),sQuery(id+"F0.wireOp",EDGE,"E19.8.11"),sQuery(id+"F0.wireOp",EDGE,"E19.8.24"),sQuery(id+"F0.wireOp",EDGE,"E19.8.25"),sQuery(id+"F0.wireOp",EDGE,"E19.9.6"),sQuery(id+"F0.wireOp",EDGE,"E19.9.8"),sQuery(id+"F0.wireOp",EDGE,"E19.9.11"),sQuery(id+"F0.wireOp",EDGE,"E19.9.24"),sQuery(id+"F0.wireOp",EDGE,"E19.9.25"),sQuery(id+"F0.wireOp",EDGE,"E19.10.6"),sQuery(id+"F0.wireOp",EDGE,"E19.10.8"),sQuery(id+"F0.wireOp",EDGE,"E19.10.11"),sQuery(id+"F0.wireOp",EDGE,"E19.10.24"),sQuery(id+"F0.wireOp",EDGE,"E19.10.25"),sQuery(id+"F0.wireOp",EDGE,"E19.11.6"),sQuery(id+"F0.wireOp",EDGE,"E19.11.8"),sQuery(id+"F0.wireOp",EDGE,"E19.11.11"),sQuery(id+"F0.wireOp",EDGE,"E19.11.24"),sQuery(id+"F0.wireOp",EDGE,"E19.11.25"),sQuery(id+"F0.wireOp",EDGE,"E19.12.6"),sQuery(id+"F0.wireOp",EDGE,"E19.12.8"),sQuery(id+"F0.wireOp",EDGE,"E19.12.11"),sQuery(id+"F0.wireOp",EDGE,"E19.12.24"),sQuery(id+"F0.wireOp",EDGE,"E19.12.25"),sQuery(id+"F0.wireOp",EDGE,"E19.13.6"),sQuery(id+"F0.wireOp",EDGE,"E19.13.8"),sQuery(id+"F0.wireOp",EDGE,"E19.13.11"),sQuery(id+"F0.wireOp",EDGE,"E19.13.24"),sQuery(id+"F0.wireOp",EDGE,"E19.13.25"),sQuery(id+"F0.wireOp",EDGE,"E19.14.6"),sQuery(id+"F0.wireOp",EDGE,"E19.14.8"),sQuery(id+"F0.wireOp",EDGE,"E19.14.11"),sQuery(id+"F0.wireOp",EDGE,"E19.14.24"),sQuery(id+"F0.wireOp",EDGE,"E19.14.25"),sQuery(id+"F0.wireOp",EDGE,"E19.15.6"),sQuery(id+"F0.wireOp",EDGE,"E19.15.8"),sQuery(id+"F0.wireOp",EDGE,"E19.15.11"),sQuery(id+"F0.wireOp",EDGE,"E19.15.24"),sQuery(id+"F0.wireOp",EDGE,"E19.15.25"),sQuery(id+"F0.wireOp",EDGE,"E19.16.6"),sQuery(id+"F0.wireOp",EDGE,"E19.16.8"),sQuery(id+"F0.wireOp",EDGE,"E19.16.11"),sQuery(id+"F0.wireOp",EDGE,"E19.16.24"),sQuery(id+"F0.wireOp",EDGE,"E19.16.25"),sQuery(id+"F0.wireOp",EDGE,"E19.17.6"),sQuery(id+"F0.wireOp",EDGE,"E19.17.8"),sQuery(id+"F0.wireOp",EDGE,"E19.17.11"),sQuery(id+"F0.wireOp",EDGE,"E19.17.24"),sQuery(id+"F0.wireOp",EDGE,"E19.17.25"),sQuery(id+"F0.wireOp",EDGE,"E19.18.6"),sQuery(id+"F0.wireOp",EDGE,"E19.18.8"),sQuery(id+"F0.wireOp",EDGE,"E19.18.11"),sQuery(id+"F0.wireOp",EDGE,"E19.18.24"),sQuery(id+"F0.wireOp",EDGE,"E19.18.25"),sQuery(id+"F0.wireOp",EDGE,"E19.19.6"),sQuery(id+"F0.wireOp",EDGE,"E19.19.8"),sQuery(id+"F0.wireOp",EDGE,"E19.19.11"),sQuery(id+"F0.wireOp",EDGE,"E19.19.24"),sQuery(id+"F0.wireOp",EDGE,"E19.19.25"),sQuery(id+"F0.wireOp",EDGE,"E19.20.6"),sQuery(id+"F0.wireOp",EDGE,"E19.20.8"),sQuery(id+"F0.wireOp",EDGE,"E19.20.11"),sQuery(id+"F0.wireOp",EDGE,"E19.20.24"),sQuery(id+"F0.wireOp",EDGE,"E19.20.25"),sQuery(id+"F0.wireOp",EDGE,"E19.21.6"),sQuery(id+"F0.wireOp",EDGE,"E19.21.8"),sQuery(id+"F0.wireOp",EDGE,"E19.21.11"),sQuery(id+"F0.wireOp",EDGE,"E19.21.24"),sQuery(id+"F0.wireOp",EDGE,"E19.21.25"),sQuery(id+"F0.wireOp",EDGE,"E19.22.6"),sQuery(id+"F0.wireOp",EDGE,"E19.22.8"),sQuery(id+"F0.wireOp",EDGE,"E19.22.11"),sQuery(id+"F0.wireOp",EDGE,"E19.22.24"),sQuery(id+"F0.wireOp",EDGE,"E19.22.25"),sQuery(id+"F0.wireOp",EDGE,"E19.23.6"),sQuery(id+"F0.wireOp",EDGE,"E19.23.8"),sQuery(id+"F0.wireOp",EDGE,"E19.23.11"),sQuery(id+"F0.wireOp",EDGE,"E19.23.24"),sQuery(id+"F0.wireOp",EDGE,"E19.23.25"),sQuery(id+"F0.wireOp",EDGE,"E19.24.6"),sQuery(id+"F0.wireOp",EDGE,"E19.24.8"),sQuery(id+"F0.wireOp",EDGE,"E19.24.11"),sQuery(id+"F0.wireOp",EDGE,"E19.24.24"),sQuery(id+"F0.wireOp",EDGE,"E19.24.25"),sQuery(id+"F0.wireOp",EDGE,"E19.25.6"),sQuery(id+"F0.wireOp",EDGE,"E19.25.8"),sQuery(id+"F0.wireOp",EDGE,"E19.25.11"),sQuery(id+"F0.wireOp",EDGE,"E19.25.24"),sQuery(id+"F0.wireOp",EDGE,"E19.25.25"),sQuery(id+"F0.wireOp",EDGE,"E19.26.6"),sQuery(id+"F0.wireOp",EDGE,"E19.26.8"),sQuery(id+"F0.wireOp",EDGE,"E19.26.11"),sQuery(id+"F0.wireOp",EDGE,"E19.26.24"),sQuery(id+"F0.wireOp",EDGE,"E19.26.25"),sQuery(id+"F0.wireOp",EDGE,"E19.27.6"),sQuery(id+"F0.wireOp",EDGE,"E19.27.8"),sQuery(id+"F0.wireOp",EDGE,"E19.27.11"),sQuery(id+"F0.wireOp",EDGE,"E19.27.24"),sQuery(id+"F0.wireOp",EDGE,"E19.27.25"),sQuery(id+"F0.wireOp",EDGE,"E19.28.6"),sQuery(id+"F0.wireOp",EDGE,"E19.28.8"),sQuery(id+"F0.wireOp",EDGE,"E19.28.11"),sQuery(id+"F0.wireOp",EDGE,"E19.28.24"),sQuery(id+"F0.wireOp",EDGE,"E19.28.25"),sQuery(id+"F0.wireOp",EDGE,"E19.29.6"),sQuery(id+"F0.wireOp",EDGE,"E19.29.8"),sQuery(id+"F0.wireOp",EDGE,"E19.29.11"),sQuery(id+"F0.wireOp",EDGE,"E19.29.24"),sQuery(id+"F0.wireOp",EDGE,"E19.29.25"),sQuery(id+"F0.wireOp",EDGE,"E21.MirrorCS"),sQuery(id+"F0.wireOp",EDGE,"E22.MirrorCS"),sQuery(id+"F0.wireOp",EDGE,"E23.trimOffspring"),sQuery(id+"F0.wireOp",EDGE,"E25.MirrorCS"),sQuery(id+"F0.wireOp",EDGE,"E26.MirrorCS"),sQuery(id+"F0.wireOp",EDGE,"E27.MirrorCS"),sQuery(id+"F0.wireOp",EDGE,"E28.MirrorCS"),sQuery(id+"F0.wireOp",EDGE,"E29.MirrorCS"),sQuery(id+"F0.wireOp",EDGE,"E30.MirrorCS"),sQuery(id+"F0.wireOp",EDGE,"E31.MirrorCS"),sQuery(id+"F0.wireOp",EDGE,"E32.MirrorCS"),sQuery(id+"F0.wireOp",EDGE,"E33.MirrorCS"),sQuery(id+"F0.wireOp",EDGE,"E34.MirrorCS"),sQuery(id+"F0.wireOp",EDGE,"E35.MirrorCS"),sQuery(id+"F0.wireOp",EDGE,"E36.MirrorCS"),sQuery(id+"F0.wireOp",EDGE,"E37.MirrorCS"),sQuery(id+"F0.wireOp",EDGE,"E38.MirrorCS"),sQuery(id+"F0.wireOp",EDGE,"E39.MirrorCS"),sQuery(id+"F0.wireOp",EDGE,"E40.MirrorCS"),sQuery(id+"F0.wireOp",EDGE,"E41.MirrorCS"),sQuery(id+"F0.wireOp",EDGE,"E42.MirrorCS"),sQuery(id+"F0.wireOp",EDGE,"E44.MirrorCS"),sQuery(id+"F0.wireOp",EDGE,"E45.MirrorCS"),sQuery(id+"F0.wireOp",EDGE,"E46.MirrorCS"),sQuery(id+"F0.wireOp",EDGE,"E47.MirrorCS"),sQuery(id+"F0.wireOp",EDGE,"E48.MirrorCS"),sQuery(id+"F0.wireOp",EDGE,"E49.MirrorCS"),sQuery(id+"F0.wireOp",EDGE,"E50.MirrorCS"),sQuery(id+"F0.wireOp",EDGE,"E51.MirrorCS"),sQuery(id+"F0.wireOp",EDGE,"E52.MirrorCS"),sQuery(id+"F0.wireOp",EDGE,"E53.MirrorCS"),sQuery(id+"F0.wireOp",EDGE,"E54.MirrorCS"),sQuery(id+"F0.wireOp",EDGE,"E55.MirrorCS"),sQuery(id+"F0.wireOp",EDGE,"E56.MirrorCS"),sQuery(id+"F0.wireOp",EDGE,"E57.MirrorCS"),sQuery(id+"F0.wireOp",EDGE,"E58.MirrorCS"),sQuery(id+"F0.wireOp",EDGE,"E59.MirrorCS"),sQuery(id+"F0.wireOp",EDGE,"E60.MirrorCS"),sQuery(id+"F0.wireOp",EDGE,"E61.MirrorCS"),sQuery(id+"F0.wireOp",EDGE,"E62.MirrorCS"),sQuery(id+"F0.wireOp",EDGE,"E63.MirrorCS"),sQuery(id+"F0.wireOp",EDGE,"E64.MirrorCS"),sQuery(id+"F0.wireOp",EDGE,"E65.MirrorCS"),sQuery(id+"F0.wireOp",EDGE,"E66.MirrorCS"),sQuery(id+"F0.wireOp",EDGE,"E67.MirrorCS"),sQuery(id+"F0.wireOp",EDGE,"E68.MirrorCS"),sQuery(id+"F0.wireOp",EDGE,"E69.MirrorCS"),sQuery(id+"F0.wireOp",EDGE,"E70.MirrorCS"),sQuery(id+"F0.wireOp",EDGE,"E71.MirrorCS"),sQuery(id+"F0.wireOp",EDGE,"E72.MirrorCS"),sQuery(id+"F0.wireOp",EDGE,"E73.MirrorCS"),sQuery(id+"F0.wireOp",EDGE,"E74.MirrorCS"),sQuery(id+"F0.wireOp",EDGE,"E75.MirrorCS"),sQuery(id+"F0.wireOp",EDGE,"E76.MirrorCS"),sQuery(id+"F0.wireOp",EDGE,"E77.MirrorCS"),sQuery(id+"F0.wireOp",EDGE,"E78.MirrorCS"),sQuery(id+"F0.wireOp",EDGE,"E79.MirrorCS"),sQuery(id+"F0.wireOp",EDGE,"E80.MirrorCS"),sQuery(id+"F0.wireOp",EDGE,"E81.MirrorCS"),sQuery(id+"F0.wireOp",EDGE,"E82.trimOffspring"),sQuery(id+"F0.wireOp",EDGE,"E83.trimOffspring")])],"isStart":false});
            var sketch = newSketch(context, id + "F2", { "sketchPlane" : qUnion([Q0])});
            skCircle(sketch, "E84", {"center": v(0, 0) * mm, "radius": 27.5 * mm});
            skSolve(sketch);
        }
        {
            var Q0;
            Q0 = qSketchRegion(id + "F2", true);
            extrude(context, id + "F3", {"entities" : qUnion([Q0]), "operationType" : NewBodyOperationType.ADD, "depth" : 15 * mm, "offsetDistance" : 25 * mm});
        }
        {
            var Q0;
            Q0=makeQuery(id+"F3.opExtrude","CAP_FACE",FACE,{"disambiguationData":[OSD([sQuery(id+"F2.wireOp",EDGE,"E84")])],"isStart":false});
            var sketch = newSketch(context, id + "F4", { "sketchPlane" : qUnion([Q0])});
            skCircle(sketch, "E85", {"center": v(0, 0) * mm, "radius": 7 * mm});
            skSolve(sketch);
        }
        {
            var Q0;
            Q0 = qSketchRegion(id + "F4", true);
            extrude(context, id + "F5", {"entities" : qUnion([Q0]), "operationType" : NewBodyOperationType.REMOVE, "endBound" : BoundingType.UP_TO_NEXT, "oppositeDirection" : true, "depth" : 25 * mm, "offsetDistance" : 25 * mm});
        }
        {
            var Q0;
            Q0=makeQuery(id+"F3.opExtrude","SWEPT_FACE",FACE,{"disambiguationData":[OSD([sQuery(id+"F2.wireOp",EDGE,"E84")])]});
            var Q1;
            Q1=makeQuery(id+"F5.boolean.opBoolean","COPY",FACE,{"derivedFrom":makeQuery(id+"F5.opExtrude","SWEPT_FACE",FACE,{"disambiguationData":[OSD([sQuery(id+"F4.wireOp",EDGE,"E85")])]})});
            chamfer(context, id + "F6", {"entities" : qUnion([Q0, Q1]), "width" : 1 * mm, "tangentPropagation" : true});
        }
    });
